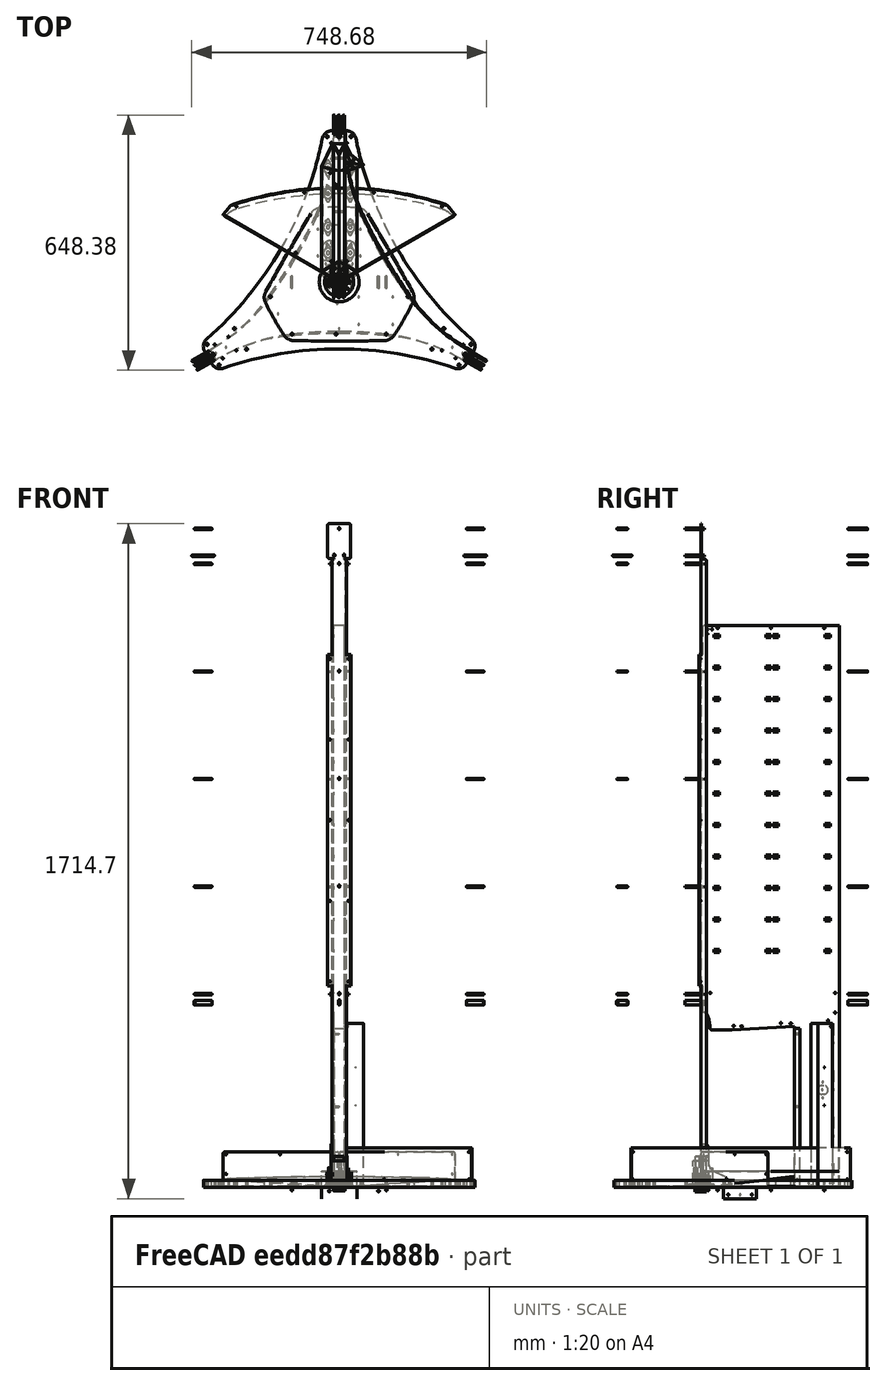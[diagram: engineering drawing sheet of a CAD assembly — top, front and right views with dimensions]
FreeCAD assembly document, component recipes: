
FREECAD ASSEMBLY — COMPONENT RECIPES ("composit_full_size3")

This assembly document has 76 components, labeled P0..P75 below (a component is one placed body or linked part). 73 of them carry a construction recipe — the FreeCAD feature program that regenerates the part from scratch, quoted from this document or its linked companion documents; the rest are supplied as boundary geometry only. No exploded tour is included for this assembly.
NOTE — document 3 of 3 of this assembly tour. The two overview renders and the header above are repeated from document 1; the component sections below continue where the previous document stopped.
COMPONENT P61 — recipe-attached ("basement2_proxy001", modeled in this document).
Construction recipe (the document's own serialized feature program — sketch geometry with constraints, then the solid features built on it; lengths are millimeters unless a unit is written):

FEATURE [PartDesign::SubShapeBinder] Binder004
  BindCopyOnChange = 0
  BindMode = 0
  ClaimChildren = true
  Context = -> Body009 [Binder004.]
  Fuse = false
  MakeFace = true
  Offset = 2
  OffsetFill = false
  OffsetIntersection = false
  OffsetJoinType = 0
  OffsetOpenResult = false
  PartialLoad = false
  Relative = false
  Support = -> [Array002]
  _Version = 2
FEATURE [PartDesign::Pad] Pad004
  Direction = (0,0,1)
  Length = 3
  Length2 = 10
  Profile = -> Binder004
  Suppressed = false
  Type = 0
FEATURE [PartDesign::SubShapeBinder] Binder134
  BindCopyOnChange = 0
  BindMode = 0
  ClaimChildren = false
  Context = -> Body009 [Binder134.]
  Fuse = false
  MakeFace = true
  OffsetFill = false
  OffsetIntersection = false
  OffsetJoinType = 0
  OffsetOpenResult = false
  PartialLoad = false
  Relative = true
  Support = -> [Body007[Pocket112.Sketch178.]]
  _Version = 2
FEATURE [PartDesign::Boolean] Boolean029
  BaseFeature = -> Pad004
  Group = -> [Compound071]
  Suppressed = false
  Type = 1
  UsePlacement = false
FEATURE [PartDesign::CoordinateSystem] Local_CS012  label="basement_bottom_proxy_bottom"
  AttacherType = Attacher::AttachEngine3D
  AttachmentSupport = -> [XY_Plane013]
  MapMode = 5
FEATURE [PartDesign::CoordinateSystem] Local_CS013  label="basement_bottom_proxy_top"
  AttacherType = Attacher::AttachEngine3D
  AttachmentOffset = pos=(0,0,3) rot=(0,0,1;0rad)
  AttachmentSupport = -> [XY_Plane013]
  MapMode = 5
  Placement = pos=(0,0,3) rot=(0,0,1;0rad)
FEATURE [PartDesign::CoordinateSystem] Local_CS016  label="basement_bottom_proxy_pillar_back_LCS"
  AttacherType = Attacher::AttachEngine3D
  AttachmentOffset = pos=(0,384,3) rot=(0,0,-1;3.14159rad)
  AttachmentSupport = -> [XY_Plane013]
  MapMode = 5
  Placement = pos=(0,384,3) rot=(0,0,-1;3.14159rad)
  expr: .AttachmentOffset.Base.y = <<pillar_placement>>.Placement.Base.y
FEATURE [PartDesign::CoordinateSystem] Local_CS023  label="basement_bottom_proxy_pillar_left_LCS"
  AttacherType = Attacher::AttachEngine3D
  AttachmentOffset = pos=(-332.554,-192,3) rot=(0,0,-1;1.0472rad)
  AttachmentSupport = -> [XY_Plane013]
  MapMode = 5
  Placement = pos=(-332.554,-192,3) rot=(0,0,-1;1.0472rad)
  expr: .AttachmentOffset.Base.x = <<pillar_placement>>.Placement.Base.y * cos(210)
  expr: .AttachmentOffset.Base.y = <<pillar_placement>>.Placement.Base.y * sin(210)
FEATURE [PartDesign::CoordinateSystem] Local_CS024  label="basement_bottom_proxy_pillar_right_LCS"
  AttacherType = Attacher::AttachEngine3D
  AttachmentOffset = pos=(332.554,-192,3) rot=(0,0,1;1.0472rad)
  AttachmentSupport = -> [XY_Plane013]
  MapMode = 5
  Placement = pos=(332.554,-192,3) rot=(0,0,1;1.0472rad)
  expr: .AttachmentOffset.Base.x = <<pillar_placement>>.Placement.Base.y * cos(330)
  expr: .AttachmentOffset.Base.y = <<pillar_placement>>.Placement.Base.y * sin(330)
FEATURE [PartDesign::Body] Body009  label="basement_bottom_proxy"
  AllowCompound = false
  Group = -> [Binder004,Pad004,Binder134,Boolean029,Local_CS012,Local_CS013,Local_CS016,Local_CS023,Local_CS024]
  Origin = -> Origin013
  Tip = -> Boolean029
COMPONENT P62 — recipe-attached ("sink_material_0.30ansi001", modeled in this document).
Construction recipe (the document's own serialized feature program — sketch geometry with constraints, then the solid features built on it; lengths are millimeters unless a unit is written):

FEATURE [Sketcher::SketchObject] Sketch037
  ArcFitTolerance = 0
  AttachmentSupport = -> [XY_Plane028]
  FullyConstrained = false
  MakeInternals = false
  MapMode = 5
  sketch-geometry (2):
    g0: LineSegment StartX=0 StartY=0 StartZ=0 EndX=74.4649 EndY=59.2839 EndZ=0
    g1: LineSegment StartX=0 StartY=0 StartZ=0 EndX=-93.8109 EndY=73.3435 EndZ=0
  constraints (2):
    c: Coincident(g0,g-1)
    c: Coincident(g1,g0)
FEATURE [Part::Part2DObjectPython] Line  label="sink_bend_line"  # Draft 2D object (typed FeaturePython)
  Area = 0
  AttachmentOffset = pos=(304.73,175.936,20) rot=(0,0,1;0rad)
  AttachmentSupport = -> [XY_Plane028]
  BendAngle = 6.48542
  ChamferSize = 0
  Closed = false
  End = (0,0,0)
  FaceAngle = 3.2479
  FilletRadius = 0
  Length = 352.44
  MakeFace = true
  MapMode = 5
  Placement = pos=(304.73,175.936,20) rot=(0,0,1;0rad)
  Points = (2) [(0,0,0),(-304.73,-175.936,-20)]
  Start = (304.73,175.936,20)
  Subdivisions = 0
  expr: .AttachmentOffset.Base.x = Spreadsheet.total_length * cos(30)
  expr: .AttachmentOffset.Base.y = Spreadsheet.total_length * sin(30)
  expr: BendAngle = atan2(.AttachmentOffset.Base.z; .AttachmentOffset.Base.y)
  expr: End = tuple(0; 0; 0)
  expr: FaceAngle = atan2(.AttachmentOffset.Base.z; Length)
FEATURE [PartDesign::Line] DatumLine
  AttacherType = Attacher::AttachEngineLine
  AttachmentSupport = -> [Z_Axis028]
  Length = 20
  MapMode = 29
  ResizeMode = 0
FEATURE [PartDesign::Line] DatumLine001
  AttacherType = Attacher::AttachEngineLine
  AttachmentSupport = -> [Line,X_Axis028]
  Length = 20
  MapMode = 24
  Placement = pos=(304.73,175.936,20) rot=(0.57735,-0.57735,-0.57735;2.0944rad)
  ResizeMode = 0
FEATURE [Sketcher::SketchObject] Sketch038
  ArcFitTolerance = 0
  AttachmentSupport = -> [Line]
  ExternalGeometry = -> [DatumLine001]
  FullyConstrained = false
  MakeInternals = false
  MapMode = 45
  Placement = pos=(152.365,87.9679,10) rot=(0.368581,0.6384,0.675717;2.39766rad)
  sketch-geometry (3):
    g0: LineSegment StartX=4.75e-14 StartY=4.27e-14 StartZ=0 EndX=4.75e-14 EndY=93.8582 EndZ=0
    g1: LineSegment StartX=4.75e-14 StartY=4.27e-14 StartZ=0 EndX=35.2298 EndY=3.46271 EndZ=0
    g2: ArcOfCircle CenterX=2.5 CenterY=2.75777 CenterZ=0 NormalX=0 NormalY=0 NormalZ=1 AngleXU=0 Radius=2.5 StartAngle=3.14159 EndAngle=4.81036
  constraints (9):
    c: Coincident(g0,g-1)
    c: Vertical(g0)
    c: Coincident(g1,g0)
    c: PointOnObject(g1,g-3)
    c: Angle(g-3) = 0.0979746
    c: Angle(g1,g0) = 1.47282  'bend_angle'
    c: Tangent(g2,g0) = 1.5708
    c: Tangent(g2,g1) = -1.5708
    c: Radius(g2) = 2.5
FEATURE [PartDesign::CoordinateSystem] Local_CS
  AttacherType = Attacher::AttachEngine3D
  AttachmentOffset = pos=(0,0,0) rot=(1,0,0;0.113192rad)
  AttachmentSupport = -> [XY_Plane028]
  MapMode = 5
  Placement = pos=(0,0,0) rot=(1,0,0;0.113192rad)
  expr: .AttachmentOffset.Rotation.Angle = Line.BendAngle
FEATURE [Sketcher::SketchObject] Sketch039
  ArcFitTolerance = 0
  AttachmentSupport = -> [Local_CS]
  ExternalGeometry = -> [Line,Sketch038]
  FullyConstrained = true
  MakeInternals = false
  MapMode = 5
  Placement = pos=(0,0,0) rot=(1,0,0;0.113192rad)
  sketch-geometry (3):
    g0: LineSegment StartX=2e-16 StartY=3.18954 StartZ=0 EndX=-459.172 EndY=270 EndZ=0
    g1: LineSegment StartX=2e-16 StartY=3.18954 StartZ=0 EndX=459.172 EndY=270 EndZ=0
    g2: LineSegment StartX=459.172 StartY=270 StartZ=0 EndX=-459.172 EndY=270 EndZ=0
  constraints (8):
    c: Coincident(g2,g1)
    c: DistanceY(g1) = 270
    c: Coincident(g0,g2)
    c: Symmetric(g1,g0,g-2)
    c: Coincident(g1,g0)
    c: PointOnObject(g0,g-2)
    c: Parallel(g1,g-3)
    c: PointOnObject(g-4,g1)
FEATURE [PartDesign::FeaturePython] BaseBend011  # WARN: FeaturePython — macro-defined, semantics opaque (R4)
  BendSide = 0
  BendSketch = -> Sketch039
  MidPlane = false
  Reverse = false
  Suppressed = false
  length = 100
  radius = 2
  thickness = 0.5
FEATURE [PartDesign::FeaturePython] Bend004  # WARN: FeaturePython — macro-defined, semantics opaque (R4)
  AutoMiter = false
  BaseFeature = -> BaseBend011
  BendType = 0
  LengthList = [100]
  LengthSpec = 1
  NonperforationMaxLength = 5
  Perforate = false
  PerforationAngle = 0
  PerforationInitialLength = 5
  PerforationMaxLength = 5
  ReliefFactor = 0.7
  Suppressed = false
  UseReliefFactor = false
  angle = 95.6135
  baseObject = -> BaseBend011 [Edge3,Edge8]
  bendAList = [95.6135]
  extend1 = 2
  extend2 = 0
  gap1 = 0
  gap2 = 0
  invert = true
  kfactor = 0.5
  length = 100
  maxExtendDist = 5
  minGap = 0.1
  minReliefGap = 1
  miterangle1 = 0
  miterangle2 = 0
  offset = 0
  radius = 2
  reliefType = 0
  reliefd = 1
  reliefw = 0.8
  sketchflip = false
  sketchinvert = false
  unfold = false
  expr: angle = 180 deg - Sketch038.Constraints.bend_angle
  expr: radius = BaseBend011.radius
FEATURE [Sketcher::SketchObject] Sketch040
  ArcFitTolerance = 0
  AttachmentSupport = -> [Local_CS]
  ExternalGeometry = -> [Line,Sketch038]
  FullyConstrained = true
  MakeInternals = false
  MapMode = 5
  Placement = pos=(0,0,0) rot=(1,0,0;0.113192rad)
  sketch-geometry (13):
    g0: ArcOfCircle CenterX=0 CenterY=-630 CenterZ=0 NormalX=0 NormalY=0 NormalZ=1 AngleXU=0 Radius=870 StartAngle=1.24863 EndAngle=1.89296
    g1: LineSegment [constr] StartX=0 StartY=0 StartZ=0 EndX=294.959 EndY=171.391 EndZ=0
    g2: LineSegment [constr] StartX=150.979 StartY=90.9189 StartZ=0 EndX=293.573 EndY=173.776 EndZ=0
    g3: LineSegment [constr] StartX=-294.959 StartY=171.391 StartZ=0 EndX=0 EndY=0 EndZ=0
    g4: LineSegment StartX=-294.959 StartY=171.391 StartZ=0 EndX=-464.661 EndY=270 EndZ=0
    g5: LineSegment StartX=-464.661 StartY=270 StartZ=0 EndX=464.661 EndY=270 EndZ=0
    g6: LineSegment StartX=464.661 StartY=270 StartZ=0 EndX=294.959 EndY=171.391 EndZ=0
    g7: LineSegment StartX=294.959 StartY=171.391 StartZ=0 EndX=294.075 EndY=172.911 EndZ=0
    g8: LineSegment StartX=294.075 StartY=172.911 StartZ=0 EndX=293.573 EndY=173.776 EndZ=0
    g9: LineSegment [constr] StartX=-294.959 StartY=171.391 StartZ=0 EndX=-294.959 EndY=171.391 EndZ=0
    g10: LineSegment StartX=293.573 StartY=173.776 StartZ=0 EndX=275.46 EndY=195.241 EndZ=0
    g11: LineSegment StartX=-293.573 StartY=173.776 StartZ=0 EndX=-275.46 EndY=195.241 EndZ=0
    g12: LineSegment StartX=-294.959 StartY=171.391 StartZ=0 EndX=-293.573 EndY=173.776 EndZ=0
  constraints (34):
    c: Coincident(g1,g-1)
    c: PointOnObject(g1,g-3)
    c: Coincident(g7,g1)
    c: Distance(g1) = 341.139
    c: Coincident(g2,g-4)
    c: Parallel(g2,g1)
    c: DistanceY(g0) = -630
    c: Radius(g0) = 870
    c: Coincident(g9,g3)
    c: Coincident(g3,g1)
    c: Symmetric(g9,g7,g-2)
    c: Coincident(g4,g5)
    c: Coincident(g5,g6)
    c: Parallel(g6,g2)
    c: Symmetric(g5,g4,g-2)
    c: DistanceY(g5) = 270
    c: Coincident(g2,g8)
    c: Coincident(g7,g8)
    c: Perpendicular(g1,g7)
    c: Perpendicular(g1,g8)
    c: Distance(g8) = 1
    c: Coincident(g10,g0)
    c: Coincident(g11,g0)
    c: PointOnObject(g0,g-2)
    c: Coincident(g10,g8)
    c: Coincident(g12,g9)
    c: Coincident(g4,g12)
    c: Coincident(g12,g11)
    c: Symmetric(g4,g6,g-2)
    c: Symmetric(g8,g11,g-2)
    c: Horizontal(g0,g0)
    c: Distance(g10) = 28.0862
    c: Angle(g10,g2) = 1.39626
    c: Coincident(g6,g7)
FEATURE [PartDesign::SubShapeBinder] Binder031
  BindCopyOnChange = 0
  BindMode = 0
  ClaimChildren = false
  Context = -> Part007 [Body020.Binder031.]
  Fuse = false
  MakeFace = true
  OffsetFill = false
  OffsetIntersection = false
  OffsetJoinType = 0
  OffsetOpenResult = false
  PartialLoad = false
  Relative = true
  _Version = 2
FEATURE [PartDesign::Pocket] Pocket022
  BaseFeature = -> Bend004
  Direction = (0,0.11295,-0.993601)
  Length = 2.5
  Length2 = 5
  Profile = -> Sketch040
  ReferenceAxis = -> Sketch040 [N_Axis]
  Refine = true
  Reversed = true
  Suppressed = false
  Type = 0
FEATURE [Sketcher::SketchObject] Sketch042
  ArcFitTolerance = 0
  AttachmentSupport = -> [XY_Plane028]
  FullyConstrained = true
  MakeInternals = false
  MapMode = 5
  sketch-geometry (7):
    g0: LineSegment StartX=-18.3205 StartY=-10 StartZ=0 EndX=-0.5 EndY=0.288675 EndZ=0
    g1: LineSegment StartX=18.3205 StartY=-10 StartZ=0 EndX=-18.3205 EndY=-10 EndZ=0
    g2: LineSegment [constr] StartX=1 StartY=1.5e-15 StartZ=0 EndX=-1e-16 EndY=0.57735 EndZ=0
    g3: LineSegment [constr] StartX=1.3e-15 StartY=-2.2e-15 StartZ=0 EndX=0.5 EndY=0.288675 EndZ=0
    g4: LineSegment StartX=0.5 StartY=0.288675 StartZ=0 EndX=18.3205 EndY=-10 EndZ=0
    g5: LineSegment StartX=-2.6e-15 StartY=1.1547 StartZ=0 EndX=0.5 EndY=0.288675 EndZ=0
    g6: LineSegment StartX=-0.5 StartY=0.288675 StartZ=0 EndX=-2.6e-15 EndY=1.1547 EndZ=0
  constraints (19):
    c: Coincident(g4,g1)
    c: Coincident(g1,g0)
    c: Symmetric(g4,g0,g-2)
    c: PointOnObject(g2,g-1)
    c: PointOnObject(g2,g-2)
    c: Angle(g2) = 2.61799
    c: Distance(g-1,g2) = 0.5
    c: Coincident(g3,g-1)
    c: PointOnObject(g3,g2)
    c: Angle(g3) = 0.523599
    c: PointOnObject(g2,g4)
    c: Perpendicular(g3,g5)
    c: Coincident(g4,g5)
    c: Coincident(g4,g3)
    c: PointOnObject(g5,g-2)
    c: Coincident(g6,g0)
    c: Coincident(g6,g5)
    c: Symmetric(g4,g0,g-2)
    c: DistanceY(g1) = -10
FEATURE [Sketcher::SketchObject] Sketch041
  ArcFitTolerance = 0
  AttachmentOffset = pos=(0,0,0) rot=(0,1,0;0.523599rad)
  AttachmentSupport = -> [XZ_Plane028]
  ExternalGeometry = -> [Sketch038,Sketch042,Sketch040]
  FullyConstrained = false
  MakeInternals = false
  MapMode = 5
  Placement = pos=(0,0,0) rot=(0.935113,0.250563,0.250563;1.63783rad)
  sketch-geometry (16):
    g0: LineSegment StartX=340.573 StartY=19.628 StartZ=0 EndX=340.432 EndY=22.112 EndZ=0
    g1: LineSegment [constr] StartX=175.779 StartY=12.7533 StartZ=0 EndX=340.432 EndY=22.112 EndZ=0
    g2: LineSegment StartX=0.57735 StartY=196.491 StartZ=0 EndX=638.392 EndY=196.491 EndZ=0
    g3: LineSegment StartX=638.392 StartY=196.491 StartZ=0 EndX=638.392 EndY=36.5557 EndZ=0
    g4: LineSegment StartX=638.392 StartY=36.5557 StartZ=0 EndX=340.573 EndY=19.628 EndZ=0
    g5: LineSegment StartX=340.432 StartY=22.112 StartZ=0 EndX=340.432 EndY=85 EndZ=0
    g6: LineSegment StartX=0.57735 StartY=85 StartZ=0 EndX=0.57735 EndY=196.491 EndZ=0
    g7: LineSegment StartX=335.432 StartY=90 StartZ=0 EndX=5.57735 EndY=90 EndZ=0
    g8: ArcOfCircle CenterX=5.57735 CenterY=85 CenterZ=0 NormalX=0 NormalY=0 NormalZ=1 AngleXU=0 Radius=5 StartAngle=1.5708 EndAngle=3.14159
    g9: ArcOfCircle CenterX=335.432 CenterY=85 CenterZ=0 NormalX=0 NormalY=0 NormalZ=1 AngleXU=0 Radius=5 StartAngle=2e-16 EndAngle=1.5708
    g10: GeomPoint [constr] X=340.432 Y=90 Z=0
    g11: LineSegment StartX=0.57735 StartY=0 StartZ=0 EndX=0.57735 EndY=27.6603 EndZ=0
    g12: ArcOfCircle CenterX=5 CenterY=27.6603 CenterZ=0 NormalX=0 NormalY=0 NormalZ=1 AngleXU=0 Radius=4.42265 StartAngle=3.14159 EndAngle=4.18879
    g13: ArcOfCircle CenterX=0.57735 CenterY=20 CenterZ=0 NormalX=0 NormalY=0 NormalZ=1 AngleXU=0 Radius=4.42265 StartAngle=-2.31e-14 EndAngle=1.0472
    g14: LineSegment StartX=5 StartY=20 StartZ=0 EndX=5 EndY=0 EndZ=0
    g15: LineSegment StartX=5 StartY=0 StartZ=0 EndX=0.57735 EndY=0 EndZ=0
  constraints (39):
    c: Coincident(g1,g-3)
    c: Coincident(g1,g0)
    c: Perpendicular(g-3,g1)
    c: Perpendicular(g1,g0)
    c: Coincident(g5,g0)
    c: Coincident(g6,g2)
    c: Horizontal(g2)
    c: Coincident(g2,g3)
    c: Vertical(g3)
    c: Coincident(g3,g4)
    c: Coincident(g4,g0)
    c: Parallel(g4,g1)
    c: Vertical(g5)
    c: Vertical(g6)
    c: Vertical(g6,g-4)
    c: Horizontal(g7)
    c: Tangent(g8,g7) = -1.5708
    c: Tangent(g8,g6) = 1.5708
    c: PointOnObject(g10,g5)
    c: PointOnObject(g10,g7)
    c: Tangent(g5,g9) = -1.5708
    c: Tangent(g7,g9) = -1.5708
    c: Equal(g9,g8)
    c: Coincident(g11,g-4)
    c: Vertical(g11)
    c: PointOnObject(g13,g11)
    c: PointOnObject(g14,g-1)
    c: Vertical(g14)
    c: Coincident(g15,g14)
    c: Coincident(g15,g11)
    c: Tangent(g13,g12) = 1.5708
    c: Tangent(g12,g11) = 1.5708
    c: Tangent(g14,g13) = 1.5708
    c: Equal(g13,g12)
    c: DistanceX(g14) = 5
    c: DistanceY(g13) = 20
    c: DistanceY(g7) = 90
    c: Radius(g9) = 5
    c: Coincident(g0,g-5)
FEATURE [Sketcher::SketchObject] Sketch043
  ArcFitTolerance = 0
  AttachmentSupport = -> [Local_CS]
  FullyConstrained = false
  MakeInternals = false
  MapMode = 5
  Placement = pos=(0,0,0) rot=(1,0,0;0.113192rad)
  expr: Constraints[12] = Sketch038.Constraints.bend_angle / 2
  sketch-geometry (7):
    g0: ArcOfCircle CenterX=-2.2e-14 CenterY=1.72e-14 CenterZ=0 NormalX=0 NormalY=0 NormalZ=1 AngleXU=0 Radius=19.4106 StartAngle=5.52221 EndAngle=10.1858
    g1: ArcOfCircle CenterX=17.4885 CenterY=-16.6545 CenterZ=0 NormalX=0 NormalY=0 NormalZ=1 AngleXU=0 Radius=4.73935 StartAngle=2.38062 EndAngle=3.72466
    g2: ArcOfCircle CenterX=-17.4885 CenterY=-16.6545 CenterZ=0 NormalX=0 NormalY=0 NormalZ=1 AngleXU=0 Radius=4.73935 StartAngle=5.70012 EndAngle=7.04416
    g3: LineSegment StartX=13.5322 StartY=-19.2639 StartZ=0 EndX=49.1398 EndY=-73.2508 EndZ=0
    g4: LineSegment StartX=-13.5322 StartY=-19.2639 StartZ=0 EndX=-49.1398 EndY=-73.2508 EndZ=0
    g5: LineSegment StartX=-49.1398 StartY=-73.2508 StartZ=0 EndX=49.1398 EndY=-73.2508 EndZ=0
    g6: LineSegment StartX=-86.3387 StartY=-141.994 StartZ=0 EndX=130.665 EndY=54.7259 EndZ=0
  constraints (13):
    c: Coincident(g0,g-1)
    c: Coincident(g5,g4)
    c: Coincident(g5,g3)
    c: Tangent(g3,g1) = -1.5708
    c: Tangent(g1,g0) = 1.5708
    c: Tangent(g2,g0) = 1.5708
    c: Tangent(g4,g2) = 1.5708
    c: Symmetric(g4,g3,g-2)
    c: Symmetric(g2,g1,g-2)
    c: DistanceX(g1) = 13.5322
    c: DistanceY(g1) = -19.2639
    c: Angle(g3) = -0.987729
    c: Angle(g6) = 0.736411
FEATURE [Sketcher::SketchObject] Sketch064
  ArcFitTolerance = 0
  AttachmentSupport = -> [Local_CS]
  FullyConstrained = true
  MakeInternals = false
  MapMode = 5
  Placement = pos=(0,0,0) rot=(1,0,0;0.113192rad)
  expr: Constraints[3] = <<Properties>>.rivet_d
  sketch-geometry (4):
    g0: Circle CenterX=-88.3 CenterY=228.865 CenterZ=0 NormalX=0 NormalY=0 NormalZ=1 AngleXU=0 Radius=1.7
    g1: Circle CenterX=88.3 CenterY=228.865 CenterZ=0 NormalX=0 NormalY=0 NormalZ=1 AngleXU=0 Radius=1.7
    g2: Circle CenterX=261.291 CenterY=193.3 CenterZ=0 NormalX=0 NormalY=0 NormalZ=1 AngleXU=0 Radius=1.7
    g3: Circle CenterX=-261.291 CenterY=193.3 CenterZ=0 NormalX=0 NormalY=0 NormalZ=1 AngleXU=0 Radius=1.7
  constraints (10):
    c: Equal(g2,g1)
    c: Equal(g2,g0)
    c: Equal(g2,g3)
    c: Diameter(g2) = 3.4
    c: DistanceX(g1) = 88.3
    c: DistanceY(g1) = 228.865
    c: DistanceX(g2) = 261.291
    c: DistanceY(g2) = 193.3
    c: Symmetric(g0,g1,g-2)
    c: Symmetric(g3,g2,g-2)
FEATURE [Sketcher::SketchObject] Sketch219
  ArcFitTolerance = 0
  FullyConstrained = false
  MakeInternals = false
  MapMode = 5
  Placement = pos=(0,8e-15,-6.7e-14) rot=(1,0,0;3.25479rad)
  sketch-geometry (6):
    g0: LineSegment StartX=297.803 StartY=-177.345 StartZ=0 EndX=303.917 EndY=-182.504 EndZ=0
    g1: LineSegment StartX=303.917 StartY=-182.504 StartZ=0 EndX=285.803 EndY=-203.969 EndZ=0
    g2: LineSegment StartX=285.803 StartY=-203.969 StartZ=0 EndX=276.608 EndY=-196.209 EndZ=0
    g3: LineSegment StartX=279.192 StartY=-196.205 StartZ=0 EndX=297.807 EndY=-180.398 EndZ=0
    g4: ArcOfCircle CenterX=296.513 CenterY=-178.873 CenterZ=0 NormalX=0 NormalY=0 NormalZ=1 AngleXU=0 Radius=2 StartAngle=5.41641 EndAngle=7.15307
    g5: ArcOfCircle CenterX=277.898 CenterY=-194.681 CenterZ=0 NormalX=0 NormalY=0 NormalZ=1 AngleXU=0 Radius=2 StartAngle=4.01147 EndAngle=5.41641
  constraints (13):
    c: Coincident(g0,g1)
    c: Coincident(g1,g2)
    c: Perpendicular(g1,g2)
    c: Perpendicular(g0,g1)
    c: Tangent(g4,g0) = 1.5708
    c: Tangent(g5,g2) = 1.5708
    c: Tangent(g5,g3) = -1.5708
    c: Tangent(g4,g3) = -1.5708
    c: Equal(g4,g5)
    c: Radius(g4) = 2
    c: Distance(g0) = 8
    c: Distance(g2) = 12.0319
    c: Distance(g3,g1) = 10.0593
FEATURE [PartDesign::FeaturePython] Bend033  # WARN: FeaturePython — macro-defined, semantics opaque (R4)
  AutoMiter = true
  BaseFeature = -> Pocket022
  BendType = 0
  LengthList = [10]
  LengthSpec = 0
  NonperforationMaxLength = 5
  Perforate = false
  PerforationAngle = 0
  PerforationInitialLength = 5
  PerforationMaxLength = 5
  ReliefFactor = 0.7
  Suppressed = false
  UseReliefFactor = false
  angle = 90
  baseObject = -> Pocket022 [Edge64,Edge69]
  bendAList = [90]
  extend1 = 0
  extend2 = 0
  gap1 = 0
  gap2 = 0
  invert = false
  kfactor = 0.5
  length = 10
  maxExtendDist = 5
  minGap = 0.2
  minReliefGap = 1
  miterangle1 = 0
  miterangle2 = 0
  offset = 0
  radius = 2
  reliefType = 0
  reliefd = 1
  reliefw = 0.8
  sketchflip = false
  sketchinvert = false
  unfold = true
  expr: radius = BaseBend011.radius
FEATURE [PartDesign::Pocket] Pocket131
  BaseFeature = -> Bend033
  Direction = (0,-0.11295,0.993601)
  Length = 5
  Length2 = 5
  Profile = -> Sketch219
  ReferenceAxis = -> Sketch219 [N_Axis]
  Suppressed = false
  Type = 0
FEATURE [PartDesign::Mirrored] Mirrored017
  BaseFeature = -> Pocket131
  MirrorPlane = -> YZ_Plane028
  Originals = -> [Pocket131]
  Suppressed = false
  TransformMode = 0
FEATURE [PartDesign::Pocket] Pocket024
  BaseFeature = -> Mirrored017
  Direction = (0,0,-1)
  Length = 5
  Length2 = 5
  Midplane = true
  Profile = -> Sketch042
  ReferenceAxis = -> Sketch042 [N_Axis]
  Suppressed = false
  Type = 1
FEATURE [PartDesign::FeaturePython] CornerRelief  # WARN: FeaturePython — macro-defined, semantics opaque (R4)
  BaseFeature = -> Pocket024
  ReliefSketch = 0
  Size = 6
  SizeRatio = 1.5
  Sketch = -> Sketch043
  Suppressed = false
  XOffset = 0
  YOffset = 0
  baseObject = -> Pocket024 [Edge35,Edge16]
  kfactor = 0.5
FEATURE [PartDesign::Pocket] Pocket023
  BaseFeature = -> CornerRelief
  Direction = (-0.5,0.866025,-1e-16)
  Length = 0.6
  Length2 = 5
  Profile = -> Sketch041
  ReferenceAxis = -> Sketch041 [N_Axis]
  Suppressed = false
  Type = 0
FEATURE [PartDesign::Mirrored] Mirrored002
  BaseFeature = -> Pocket023
  MirrorPlane = -> YZ_Plane028
  Originals = -> [Pocket023]
  Refine = true
  Suppressed = false
  TransformMode = 0
FEATURE [PartDesign::Boolean] Boolean008
  BaseFeature = -> Mirrored002
  Group = -> [Compound028]
  Suppressed = false
  Type = 1
  UsePlacement = false
  expr: Group = <<sink_fix001>>._self
FEATURE [PartDesign::Pocket] Pocket029
  BaseFeature = -> Boolean008
  Direction = (0,0.11295,-0.993601)
  Length = 5
  Length2 = 5
  Profile = -> Sketch064
  ReferenceAxis = -> Sketch064 [N_Axis]
  Reversed = true
  Suppressed = false
  Type = 1
FEATURE [PartDesign::Body] Body020  label="sink_material_0.30ansi"
  AllowCompound = false
  Group = -> [Sketch037,Line,DatumLine,Sketch038,DatumLine001,Sketch039,BaseBend011,Bend004,Local_CS,Sketch040,Binder031,Pocket022,Sketch041,Sketch042,Sketch219,Bend033,Pocket131,Mirrored017,Pocket024,Sketch043,CornerRelief,Pocket023,Mirrored002,Boolean008,Sketch064,Pocket029]
  Origin = -> Origin028
  Tip = -> Pocket029
COMPONENT P63 — recipe-attached ("Body110", modeled in this document).
Construction recipe (the document's own serialized feature program — sketch geometry with constraints, then the solid features built on it; lengths are millimeters unless a unit is written):

FEATURE [PartDesign::SubShapeBinder] Binder061
  BindCopyOnChange = 0
  BindMode = 0
  ClaimChildren = false
  Context = -> Part007 [Body021.Binder061.]
  Fuse = false
  MakeFace = true
  OffsetFill = false
  OffsetIntersection = false
  OffsetJoinType = 0
  OffsetOpenResult = false
  PartialLoad = false
  Relative = false
  Support = -> [Body020[Pocket022.Sketch040.]]
  _Version = 2
FEATURE [PartDesign::SubShapeBinder] Binder062
  BindCopyOnChange = 0
  BindMode = 0
  ClaimChildren = false
  Context = -> Part007 [Body021.Binder062.]
  Fuse = false
  MakeFace = true
  OffsetFill = false
  OffsetIntersection = false
  OffsetJoinType = 0
  OffsetOpenResult = false
  PartialLoad = false
  Relative = false
  Support = -> [Body020[Pocket029.Sketch064.]]
  _Version = 2
FEATURE [Sketcher::SketchObject] Sketch109
  ArcFitTolerance = 0
  AttachmentSupport = -> [XY_Plane029]
  ExternalGeometry = -> [Binder061]
  FullyConstrained = false
  MakeInternals = false
  MapMode = 5
  sketch-geometry (19):
    g0: ArcOfCircle CenterX=291.996 CenterY=172.865 CenterZ=0 NormalX=0 NormalY=0 NormalZ=1 AngleXU=0 Radius=1 StartAngle=5.23599 EndAngle=6.98132
    g1: LineSegment StartX=5.51e-14 StartY=239 StartZ=0 EndX=5.51e-14 EndY=240 EndZ=0
    g2: LineSegment StartX=292.496 StartY=171.999 StartZ=0 EndX=287.719 EndY=169.241 EndZ=0
    g3: ArcOfCircle CenterX=287.219 CenterY=170.107 CenterZ=0 NormalX=0 NormalY=0 NormalZ=1 AngleXU=0 Radius=1 StartAngle=3.90153 EndAngle=5.23599
    g4: LineSegment StartX=5.51e-14 StartY=239 StartZ=0 EndX=5.51e-14 EndY=224 EndZ=0
    g5: ArcOfCircle CenterX=243.002 CenterY=128.086 CenterZ=0 NormalX=0 NormalY=0 NormalZ=1 AngleXU=0 Radius=60 StartAngle=0.759936 EndAngle=1.27733
    g6: GeomPoint [constr] X=287.033 Y=168.845 Z=0
    g7: GeomPoint [constr] X=293.528 Y=172.595 Z=0
    g8: ArcOfCircle CenterX=1.26657 CenterY=-621.999 CenterZ=0 NormalX=0 NormalY=0 NormalZ=1 AngleXU=0 Radius=862 StartAngle=1.25533 EndAngle=1.57227
    g9: LineSegment [constr] StartX=5.28e-14 StartY=220.8 StartZ=0 EndX=5.51e-14 EndY=240 EndZ=0
    g10: ArcOfCircle [constr] CenterX=0 CenterY=-641.2 CenterZ=0 NormalX=0 NormalY=0 NormalZ=1 AngleXU=0 Radius=862 StartAngle=1.25386 EndAngle=1.5708
    g11: LineSegment [constr] StartX=5.51e-14 StartY=240 StartZ=0 EndX=268.713 EndY=197.462 EndZ=0
    g12: LineSegment [constr] StartX=5.28e-14 StartY=220.8 StartZ=0 EndX=268.65 EndY=177.867 EndZ=0
    g13: ArcOfCircle CenterX=0 CenterY=-676.059 CenterZ=0 NormalX=0 NormalY=0 NormalZ=1 AngleXU=0 Radius=900.059 StartAngle=1.27733 EndAngle=1.5708
    g14: Circle [constr] CenterX=268.65 CenterY=177.867 CenterZ=0 NormalX=0 NormalY=0 NormalZ=1 AngleXU=0 Radius=4
    g15: LineSegment [constr] StartX=0 StartY=0 StartZ=0 EndX=301.632 EndY=174.148 EndZ=0
    g16: LineSegment [constr] StartX=0 StartY=0 StartZ=0 EndX=-15 EndY=25.9808 EndZ=0
    g17: ArcOfCircle CenterX=262.507 CenterY=178.449 CenterZ=0 NormalX=0 NormalY=0 NormalZ=1 AngleXU=0 Radius=20 StartAngle=0.698132 EndAngle=1.25533
    g18: LineSegment StartX=292.762 StartY=173.508 StartZ=0 EndX=277.828 EndY=191.305 EndZ=0
  constraints (51):
    c: Tangent(g17,g8) = -1.5708
    c: Vertical(g1)
    c: PointOnObject(g1,g-2)
    c: Angle(g2) = -2.61799
    c: Tangent(g2,g0) = 1.5708
    c: DistanceY(g1,g1) = 1
    c: Tangent(g3,g2) = 1.5708
    c: Radius(g3) = 1
    c: Equal(g3,g0)
    c: Coincident(g4,g1)
    c: Vertical(g4)
    c: Distance(g4) = 15
    c: Tangent(g5,g3) = 1.5708
    c: PointOnObject(g7,g2)
    c: PointOnObject(g6,g2)
    c: PointOnObject(g6,g5)
    c: Coincident(g8,g1)
    c: PointOnObject(g9,g-2)
    c: DistanceY(g9,g4) = 3.2
    c: Coincident(g9,g1)
    c: Radius(g8) = 862  'outer_r'
    c: Distance(g6,g7) = 7.5
    c: PointOnObject(g10,g-2)
    c: Coincident(g11,g1)
    c: Coincident(g11,g17)
    c: Coincident(g12,g10)
    c: Coincident(g12,g10)
    c: Equal(g10,g8)
    c: Equal(g12,g11)
    c: Coincident(g10,g9)
    c: PointOnObject(g13,g-2)
    c: Coincident(g13,g4)
    c: Tangent(g13,g5) = -1.5708
    c: Coincident(g14,g10)
    c: Tangent(g14,g5)
    c: Radius(g14) = 4
    c: Coincident(g15,g-1)
    c: Angle(g15) = 0.523599
    c: Distance(g6,g15) = 2.7076
    c: DistanceY(g1) = 240
    c: Coincident(g16,g15)
    c: Perpendicular(g15,g16)
    c: Distance(g7,g16) = 340.5
    c: Tangent(g18,g0) = -1.5708
    c: Angle(g18) = 2.26893
    c: Tangent(g17,g18) = -1.5708
    c: PointOnObject(g8,g-5)
    c: Radius(g17) = 20
    c: PointOnObject(g7,g18)
    c: Radius(g5) = 60
    c: Distance(g16) = 30
FEATURE [PartDesign::Pad] Pad014
  Direction = (0,0,1)
  Length = 3
  Length2 = 10
  Profile = -> Sketch109
  ReferenceAxis = -> Sketch109 [N_Axis]
  Suppressed = false
  Type = 0
FEATURE [PartDesign::Mirrored] Mirrored008
  BaseFeature = -> Pad014
  MirrorPlane = -> Sketch109 [V_Axis]
  Originals = -> [Pad014]
  Refine = true
  Suppressed = false
  TransformMode = 0
FEATURE [PartDesign::Pocket] Pocket055
  BaseFeature = -> Mirrored008
  Direction = (0,0,-1)
  Length = 5
  Length2 = 5
  Profile = -> Binder062
  Reversed = true
  Suppressed = false
  Type = 0
FEATURE [PartDesign::Body] Body021
  AllowCompound = false
  Group = -> [Binder061,Binder062,Sketch109,Pad014,Mirrored008,Pocket055]
  Origin = -> Origin029
  Placement = pos=(0,0,0) rot=(1,0,0;0.116239rad)
  Tip = -> Pocket055
COMPONENT P64 — recipe-attached ("hat003", modeled in this document).
Construction recipe (the document's own serialized feature program — sketch geometry with constraints, then the solid features built on it; lengths are millimeters unless a unit is written):

FEATURE [PartDesign::SubShapeBinder] Binder041
  BindCopyOnChange = 0
  BindMode = 0
  ClaimChildren = true
  Context = -> Body076 [Binder041.]
  Fuse = false
  MakeFace = true
  OffsetFill = false
  OffsetIntersection = false
  OffsetJoinType = 0
  OffsetOpenResult = false
  PartialLoad = false
  Relative = false
  Support = -> [Array006]
  _Version = 2
FEATURE [PartDesign::Pad] Pad010
  Direction = (0,0,1)
  Length = 0.3
  Length2 = 10
  Profile = -> Binder041
  Suppressed = false
  Type = 0
FEATURE [Sketcher::SketchObject] Sketch072
  ArcFitTolerance = 0
  AttachmentSupport = -> [XY_Plane039]
  FullyConstrained = true
  MakeInternals = false
  MapMode = 5
  sketch-geometry (3):
    g0: Circle CenterX=122.567 CenterY=-102.846 CenterZ=0 NormalX=0 NormalY=0 NormalZ=1 AngleXU=0 Radius=15
    g1: Circle CenterX=-122.567 CenterY=-102.846 CenterZ=0 NormalX=0 NormalY=0 NormalZ=1 AngleXU=0 Radius=15
    g2: LineSegment [constr] StartX=0 StartY=0 StartZ=0 EndX=122.567 EndY=-102.846 EndZ=0
  constraints (7):
    c: Coincident(g2,g-1)
    c: Coincident(g2,g0)
    c: Angle(g2) = -0.698132
    c: Symmetric(g1,g0,g-2)
    c: Equal(g0,g1)
    c: Distance(g2) = 160
    c: Diameter(g0) = 30
FEATURE [PartDesign::Boolean] Boolean063
  BaseFeature = -> Pad010
  Group = -> [Compound116]
  Suppressed = false
  Type = 1
  UsePlacement = false
FEATURE [PartDesign::FeaturePython] Bend032  # WARN: FeaturePython — macro-defined, semantics opaque (R4)
  AutoMiter = true
  BaseFeature = -> Boolean063
  BendType = 0
  LengthList = [25]
  LengthSpec = 0
  NonperforationMaxLength = 5
  Perforate = false
  PerforationAngle = 0
  PerforationInitialLength = 5
  PerforationMaxLength = 5
  ReliefFactor = 0.7
  Suppressed = false
  UseReliefFactor = false
  angle = 90
  baseObject = -> Boolean063 [Edge33,Edge35]
  bendAList = [90]
  extend1 = 0
  extend2 = 0
  gap1 = 3.2
  gap2 = 3.2
  invert = false
  kfactor = 0.5
  length = 25
  maxExtendDist = 5
  minGap = 0.2
  minReliefGap = 1
  miterangle1 = 0
  miterangle2 = 0
  offset = 0
  radius = 0.1
  reliefType = 0
  reliefd = 1
  reliefw = 0.8
  sketchflip = false
  sketchinvert = false
  unfold = false
FEATURE [PartDesign::Boolean] Boolean064
  BaseFeature = -> Bend032
  Group = -> [Fusion011]
  Suppressed = false
  Type = 1
  UsePlacement = false
FEATURE [PartDesign::Body] Body076  label="hat_top"
  AllowCompound = false
  Group = -> [Binder041,Pad010,Sketch072,Boolean063,Bend032,Boolean064]
  Origin = -> Origin039
  Placement = pos=(0,0,87) rot=(0,0,1;0rad)
  Tip = -> Boolean064
COMPONENT P65 — recipe-attached ("hat004", modeled in this document).
Construction recipe (the document's own serialized feature program — sketch geometry with constraints, then the solid features built on it; lengths are millimeters unless a unit is written):

FEATURE [PartDesign::SubShapeBinder] Binder039
  BindCopyOnChange = 0
  BindMode = 0
  ClaimChildren = true
  Context = -> Body075 [Binder039.]
  Fuse = false
  MakeFace = true
  OffsetFill = false
  OffsetIntersection = false
  OffsetJoinType = 0
  OffsetOpenResult = false
  PartialLoad = false
  Relative = false
  Support = -> [Array005]
  _Version = 2
FEATURE [PartDesign::Pad] Pad009
  Direction = (0,0,1)
  Length = 0.3
  Length2 = 10
  Profile = -> Binder039
  Suppressed = false
  Type = 0
FEATURE [PartDesign::SubShapeBinder] Binder040
  BindCopyOnChange = 0
  BindMode = 0
  ClaimChildren = true
  Context = -> Part010 [Body075.Binder040.]
  Fuse = false
  MakeFace = true
  OffsetFill = false
  OffsetIntersection = false
  OffsetJoinType = 0
  OffsetOpenResult = false
  PartialLoad = false
  Placement = pos=(0,382,0) rot=(0,0,1;3.14159rad)
  Relative = false
  Support = -> [Sketch066]
  _Version = 2
  expr: Support = Sketch066._self
FEATURE [PartDesign::Pocket] Pocket032
  BaseFeature = -> Pad009
  Direction = (0,0,-1)
  Length = 5
  Length2 = 5
  Midplane = true
  Profile = -> Binder040
  Suppressed = false
  Type = 1
FEATURE [Sketcher::SketchObject] Sketch098
  ArcFitTolerance = 0
  AttachmentSupport = -> [XY_Plane038]
  FullyConstrained = true
  MakeInternals = false
  MapMode = 5
  sketch-geometry (1):
    g0: Circle CenterX=0 CenterY=0 CenterZ=0 NormalX=0 NormalY=0 NormalZ=1 AngleXU=0 Radius=3.25
  constraints (2):
    c: Coincident(g0,g-1)
    c: Diameter(g0) = 6.5
FEATURE [Sketcher::SketchObject] Sketch108
  ArcFitTolerance = 0
  AttachmentSupport = -> [XY_Plane038]
  ExternalGeometry = -> [Binder039]
  FullyConstrained = true
  MakeInternals = false
  MapMode = 5
  expr: Constraints[3] = <<Properties>>.rivet_d
  sketch-geometry (2):
    g0: LineSegment [constr] StartX=112.627 StartY=65.0251 StartZ=0 EndX=101.801 EndY=58.7751 EndZ=0
    g1: Circle CenterX=101.801 CenterY=58.7751 CenterZ=0 NormalX=0 NormalY=0 NormalZ=1 AngleXU=0 Radius=1.7
  constraints (5):
    c: Coincident(g0,g-3)
    c: PointOnObject(g-1,g0)
    c: Coincident(g1,g0)
    c: Diameter(g1) = 3.4
    c: Distance(g0) = 12.5
FEATURE [PartDesign::Pocket] Pocket054
  BaseFeature = -> Pocket032
  Direction = (0,0,-1)
  Length = 5
  Length2 = 5
  Profile = -> Sketch108
  ReferenceAxis = -> Sketch108 [N_Axis]
  Reversed = true
  Suppressed = false
  Type = 0
FEATURE [PartDesign::PolarPattern] PolarPattern
  Angle = 360
  Axis = -> Z_Axis038
  BaseFeature = -> Pocket054
  Mode = 0
  Occurrences = 3
  Offset = 120
  Originals = -> [Pocket032,Pocket054]
  Suppressed = false
  TransformMode = 0
FEATURE [PartDesign::Hole] Hole015
  BaseFeature = -> PolarPattern
  CustomThreadClearance = 0
  Depth = 25
  DepthType = 0
  Diameter = 27.5
  DrillForDepth = false
  DrillPoint = 1
  DrillPointAngle = 118
  HoleCutCountersinkAngle = 90
  HoleCutCustomValues = false
  HoleCutDepth = 0
  HoleCutDiameter = 0
  HoleCutType = 0
  ModelThread = false
  Profile = -> Sketch098
  Reversed = true
  Suppressed = false
  Tapered = false
  TaperedAngle = 90
  ThreadClass = 0
  ThreadDepth = 23.5
  ThreadDepthType = 0
  ThreadDirection = 0
  ThreadFit = 0
  ThreadSize = 0
  ThreadType = 0
  Threaded = false
  UseCustomThreadClearance = false
  expr: Diameter = <<sleeve_inner_sketch>>.Constraints.outer_r * 2 + 1.5 mm
FEATURE [PartDesign::SubShapeBinder] Binder054  label="socket_fixture"
  BindCopyOnChange = 0
  BindMode = 0
  ClaimChildren = false
  Context = -> Part010 [Body075.Binder054.]
  Fuse = false
  MakeFace = true
  OffsetFill = false
  OffsetIntersection = false
  OffsetJoinType = 0
  OffsetOpenResult = false
  PartialLoad = false
  Placement = pos=(69,65,0) rot=(0,0,1;3.14159rad)
  Relative = false
  Support = -> [<external socket_fixture.FCStd>#Sketch003]
  _Version = 2
  expr: Support = socket_fixture#<<fix_holes>>._self
FEATURE [PartDesign::SubShapeBinder] Binder055  label="driver_fixture"
  BindCopyOnChange = 0
  BindMode = 0
  ClaimChildren = false
  Context = -> Part010 [Body075.Binder055.]
  Fuse = false
  MakeFace = true
  OffsetFill = false
  OffsetIntersection = false
  OffsetJoinType = 0
  OffsetOpenResult = false
  PartialLoad = false
  Placement = pos=(-24,152,0) rot=(0,0,1;0rad)
  Relative = false
  Support = -> [<external UET-VAS-060A20_12V_IP20.FCStd>#Sketch001]
  _Version = 2
  expr: Support = <<UET-VAS-060A20_12V_IP20>>#<<holes>>._self
FEATURE [PartDesign::SubShapeBinder] Binder135
  BindCopyOnChange = 0
  BindMode = 0
  ClaimChildren = false
  Context = -> Part010 [Body075.Binder135.]
  Fuse = false
  MakeFace = true
  OffsetFill = false
  OffsetIntersection = false
  OffsetJoinType = 0
  OffsetOpenResult = false
  PartialLoad = false
  Placement = pos=(35,150,0) rot=(0,0,1;0rad)
  Relative = false
  Support = -> [Sketch226]
  _Version = 2
  expr: Support = <<UV_driver_holder_holes_Sketch>>._self
FEATURE [PartDesign::Boolean] Boolean035
  BaseFeature = -> Hole015
  Group = -> [Compound084]
  Suppressed = false
  Type = 1
  UsePlacement = false
FEATURE [PartDesign::Body] Body075  label="hat_bottom_material_0.30ansi"
  AllowCompound = false
  Group = -> [Binder039,Pad009,Binder040,Pocket032,Pocket054,PolarPattern,Sketch098,Hole015,Binder054,Binder055,Sketch108,Binder135,Boolean035]
  Origin = -> Origin038
  Tip = -> Boolean035
COMPONENT P66 — recipe-attached ("hat_plexiglass_material_0.30ansi001", modeled in this document).
Construction recipe (the document's own serialized feature program — sketch geometry with constraints, then the solid features built on it; lengths are millimeters unless a unit is written):

FEATURE [PartDesign::SubShapeBinder] Binder048
  BindCopyOnChange = 0
  BindMode = 0
  ClaimChildren = true
  Context = -> Part010 [Body078.Binder048.]
  Fuse = false
  MakeFace = true
  OffsetFill = false
  OffsetIntersection = false
  OffsetJoinType = 0
  OffsetOpenResult = false
  PartialLoad = false
  Relative = false
  Support = -> [Compound043]
  _Version = 2
FEATURE [PartDesign::FeaturePython] BaseBend022  # WARN: FeaturePython — macro-defined, semantics opaque (R4)
  BendSide = 1
  BendSketch = -> Binder048
  MidPlane = false
  Reverse = false
  Suppressed = false
  length = 96
  radius = 1
  thickness = 1.5
FEATURE [PartDesign::SubShapeBinder] Binder049
  BindCopyOnChange = 0
  BindMode = 0
  ClaimChildren = true
  Context = -> Part010 [Body078.Binder049.]
  Fuse = false
  MakeFace = false
  OffsetFill = false
  OffsetIntersection = false
  OffsetJoinType = 0
  OffsetOpenResult = false
  PartialLoad = false
  Placement = pos=(0,362,6) rot=(0.57735,0.57735,0.57735;2.0944rad)
  Relative = false
  Support = -> [Sketch073]
  _Version = 2
  expr: Support = Sketch073._self
FEATURE [PartDesign::Plane] DatumPlane003
  AttachmentOffset = pos=(0,0,0) rot=(0,1,0;0.523599rad)
  AttachmentSupport = -> [XZ_Plane043]
  Length = 648.977
  MapMode = 5
  Placement = pos=(0,0,0) rot=(0.935113,0.250563,0.250563;1.63783rad)
  ResizeMode = 0
  Width = 174.677
FEATURE [PartDesign::Hole] Hole010
  BaseFeature = -> BaseBend022
  CustomThreadClearance = 0
  Depth = 1303.68
  DepthType = 1
  Diameter = 3.4
  DrillForDepth = false
  DrillPoint = 1
  DrillPointAngle = 118
  HoleCutCountersinkAngle = 90
  HoleCutCustomValues = false
  HoleCutDepth = 0
  HoleCutDiameter = 6.1
  HoleCutType = 0
  ModelThread = false
  Profile = -> Binder049
  Reversed = true
  Suppressed = false
  Tapered = false
  TaperedAngle = 90
  ThreadClass = 0
  ThreadDepth = 1303.68
  ThreadDepthType = 0
  ThreadDirection = 0
  ThreadFit = 0
  ThreadSize = 0
  ThreadType = 0
  Threaded = false
  UseCustomThreadClearance = false
  expr: Diameter = <<Properties>>.rivet_d
FEATURE [Sketcher::SketchObject] Sketch081
  ArcFitTolerance = 0
  AttachmentOffset = pos=(0,0,0) rot=(0,1,0;-1.0472rad)
  AttachmentSupport = -> [XZ_Plane043]
  FullyConstrained = true
  MakeInternals = false
  MapMode = 5
  Placement = pos=(0,0,0) rot=(-0.774597,0.447214,0.447214;4.45971rad)
  expr: Constraints[2] = <<Properties>>.rivet_d
  sketch-geometry (1):
    g0: Circle CenterX=0 CenterY=19 CenterZ=0 NormalX=0 NormalY=0 NormalZ=1 AngleXU=0 Radius=1.7
  constraints (3):
    c: PointOnObject(g0,g-2)
    c: DistanceY(g0) = 19
    c: Diameter(g0) = 3.4
FEATURE [PartDesign::Mirrored] Mirrored005
  BaseFeature = -> Hole010
  MirrorPlane = -> DatumPlane003
  Originals = -> [Hole010]
  Refine = true
  Suppressed = false
  TransformMode = 0
FEATURE [PartDesign::SubShapeBinder] Binder050
  BindCopyOnChange = 0
  BindMode = 0
  ClaimChildren = true
  Context = -> Part010 [Body078.Binder050.]
  Fuse = false
  MakeFace = true
  OffsetFill = false
  OffsetIntersection = false
  OffsetJoinType = 0
  OffsetOpenResult = false
  PartialLoad = false
  Relative = false
  Support = -> [Body075[Binder039.Array005.Compound039.Sketch068.]]
  _Version = 2
FEATURE [Sketcher::SketchObject] Sketch082
  ArcFitTolerance = 0
  AttachmentSupport = -> [XY_Plane043]
  FullyConstrained = true
  MakeInternals = false
  MapMode = 5
FEATURE [PartDesign::Pocket] Pocket117
  BaseFeature = -> Mirrored005
  Direction = (0.866025,0.5,-1e-16)
  Length = 5
  Length2 = 5
  Midplane = true
  Profile = -> Sketch081
  ReferenceAxis = -> Sketch081 [N_Axis]
  Refine = true
  Suppressed = false
  Type = 1
FEATURE [PartDesign::Body] Body078  label="hat_plexiglass_material_0.30ansi"
  AllowCompound = false
  Group = -> [Binder048,BaseBend022,Binder049,DatumPlane003,Hole010,Sketch081,Mirrored005,Binder050,Sketch082,Pocket117]
  Origin = -> Origin043
  Placement = pos=(0,0,-3) rot=(0,0,1;0rad)
  Tip = -> Pocket117
COMPONENT P67 — recipe-attached ("top_amplifier_cornrer_material_0.50ansi001", modeled in this document).
Construction recipe (the document's own serialized feature program — sketch geometry with constraints, then the solid features built on it; lengths are millimeters unless a unit is written):

FEATURE [Sketcher::SketchObject] Sketch191  label="top_corner_base_sketch"
  ArcFitTolerance = 0
  AttachmentSupport = -> [XY_Plane087]
  FullyConstrained = true
  MakeInternals = false
  MapMode = 5
  sketch-geometry (2):
    g0: LineSegment StartX=-23.3827 StartY=13.5 StartZ=0 EndX=-5.116e-13 EndY=-3.109e-13 EndZ=0
    g1: LineSegment StartX=-5.116e-13 StartY=-3.109e-13 StartZ=0 EndX=23.3827 EndY=13.5 EndZ=0
  constraints (5):
    c: Coincident(g0,g-1)
    c: Coincident(g0,g1)
    c: Symmetric(g0,g1,g-2)
    c: Angle(g1,g0) = 2.0944
    c: Distance(g1) = 27  'length'
FEATURE [PartDesign::FeaturePython] BaseBend046  # WARN: FeaturePython — macro-defined, semantics opaque (R4)
  BendSide = 0
  BendSketch = -> Sketch191
  MidPlane = false
  Reverse = false
  Suppressed = false
  length = 30
  radius = 2
  thickness = 2
FEATURE [Sketcher::SketchObject] Sketch193
  ArcFitTolerance = 0
  AttachmentOffset = pos=(0,0,0) rot=(0,1,0;0.523599rad)
  AttachmentSupport = -> [XZ_Plane087]
  FullyConstrained = true
  MakeInternals = false
  MapMode = 5
  Placement = pos=(0,0,0) rot=(0.935113,0.250563,0.250563;1.63783rad)
  expr: Constraints[6] = <<top_corner_base_sketch>>.Constraints.length
  sketch-geometry (9):
    g0: LineSegment StartX=27 StartY=20 StartZ=0 EndX=27 EndY=0 EndZ=0
    g1: LineSegment StartX=27 StartY=0 StartZ=0 EndX=4 EndY=0 EndZ=0
    g2: ArcOfCircle CenterX=24 CenterY=21.3669 CenterZ=0 NormalX=0 NormalY=0 NormalZ=1 AngleXU=0 Radius=3 StartAngle=5.42813 EndAngle=6.28319
    g3: ArcOfCircle CenterX=2.87807 CenterY=3 CenterZ=0 NormalX=0 NormalY=0 NormalZ=1 AngleXU=0 Radius=3 StartAngle=4.71239 EndAngle=5.42813
    g4: LineSegment [constr] StartX=25.9685 StartY=19.1031 StartZ=0 EndX=27 EndY=20 EndZ=0
    g5: LineSegment [constr] StartX=4 StartY=0 StartZ=0 EndX=4.84661 EndY=0.736183 EndZ=0
    g6: LineSegment StartX=4.84661 StartY=0.736183 StartZ=0 EndX=25.9685 EndY=19.1031 EndZ=0
    g7: LineSegment StartX=2.87807 StartY=0 StartZ=0 EndX=4 EndY=0 EndZ=0
    g8: LineSegment StartX=27 StartY=20 StartZ=0 EndX=27 EndY=21.3669 EndZ=0
  constraints (24):
    c: PointOnObject(g5,g-1)
    c: Coincident(g4,g0)
    c: PointOnObject(g0,g-1)
    c: Vertical(g0)
    c: Coincident(g0,g1)
    c: Coincident(g1,g5)
    c: DistanceX(g0) = 27
    c: DistanceX(g5) = 4
    c: Tangent(g2,g0)
    c: Coincident(g5,g6)
    c: Coincident(g7,g1)
    c: Horizontal(g7)
    c: Coincident(g8,g0)
    c: Coincident(g8,g2)
    c: Vertical(g8)
    c: Equal(g3,g2)
    c: Radius(g3) = 3
    c: Tangent(g3,g6) = -1.5708
    c: Tangent(g6,g2) = -1.5708
    c: Coincident(g2,g4)
    c: Parallel(g4,g6)
    c: Parallel(g5,g6)
    c: Tangent(g7,g3) = -1.5708
    c: DistanceY(g0) = 20
FEATURE [PartDesign::FeaturePython] Bend029  # WARN: FeaturePython — macro-defined, semantics opaque (R4)
  AutoMiter = true
  BaseFeature = -> BaseBend046
  BendType = 0
  LengthList = [20]
  LengthSpec = 1
  NonperforationMaxLength = 5
  Perforate = false
  PerforationAngle = 0
  PerforationInitialLength = 5
  PerforationMaxLength = 5
  ReliefFactor = 0.7
  Suppressed = false
  UseReliefFactor = false
  angle = 90
  baseObject = -> BaseBend046 [Edge17]
  bendAList = [90]
  extend1 = 0
  extend2 = 0
  gap1 = 0
  gap2 = 0
  invert = true
  kfactor = 0.5
  length = 20
  maxExtendDist = 5
  minGap = 0.1
  minReliefGap = 1
  miterangle1 = 0
  miterangle2 = 0
  offset = 0
  radius = 2
  reliefType = 0
  reliefd = 1
  reliefw = 0.8
  sketchflip = false
  sketchinvert = false
  unfold = false
  expr: radius = BaseBend046.radius
FEATURE [PartDesign::Fillet] Fillet014
  Base = -> Bend029 [Edge8,Edge40,Edge42]
  BaseFeature = -> Bend029
  Radius = 2
  SupportTransform = false
  Suppressed = false
  UseAllEdges = false
FEATURE [PartDesign::Pocket] Pocket118
  BaseFeature = -> Fillet014
  Direction = (-0.5,0.866025,-1e-16)
  Length = 5
  Length2 = 5
  Midplane = true
  Profile = -> Sketch193
  ReferenceAxis = -> Sketch193 [N_Axis]
  Suppressed = false
  Type = 1
FEATURE [PartDesign::Mirrored] Mirrored014
  BaseFeature = -> Pocket118
  MirrorPlane = -> YZ_Plane087
  Originals = -> [Pocket118]
  Suppressed = false
  TransformMode = 0
FEATURE [PartDesign::Boolean] Boolean017
  BaseFeature = -> Mirrored014
  Group = -> [Compound072]
  Refine = true
  Suppressed = false
  Type = 1
  UsePlacement = false
FEATURE [PartDesign::Body] Body113  label="top_amplifier_cornrer_material_0.50ansi"
  AllowCompound = false
  Group = -> [Sketch191,BaseBend046,Sketch193,Bend029,Fillet014,Pocket118,Mirrored014,Boolean017]
  Origin = -> Origin087
  Tip = -> Boolean017
COMPONENT P68 — recipe-attached ("sleeve_outer001", modeled in this document).
Construction recipe (the document's own serialized feature program — sketch geometry with constraints, then the solid features built on it; lengths are millimeters unless a unit is written):

FEATURE [Sketcher::SketchObject] Sketch220  label="sleeve_outer_sketch"
  ArcFitTolerance = 0
  AttachmentSupport = -> [XZ_Plane100]
  FullyConstrained = true
  MakeInternals = false
  MapMode = 5
  Placement = pos=(0,0,0) rot=(1,0,0;1.5708rad)
  expr: Constraints[13] = <<sleeve_inner_sketch>>.Constraints.outer_r + 0.25 mm
  sketch-geometry (6):
    g0: LineSegment StartX=13.25 StartY=67 StartZ=0 EndX=13.25 EndY=0 EndZ=0
    g1: LineSegment StartX=13.25 StartY=0 StartZ=0 EndX=35.25 EndY=0 EndZ=0
    g2: LineSegment StartX=35.25 StartY=0 StartZ=0 EndX=35.25 EndY=7 EndZ=0
    g3: LineSegment StartX=35.25 StartY=7 StartZ=0 EndX=20.25 EndY=7 EndZ=0
    g4: LineSegment StartX=20.25 StartY=7 StartZ=0 EndX=20.25 EndY=67 EndZ=0
    g5: LineSegment StartX=20.25 StartY=67 StartZ=0 EndX=13.25 EndY=67 EndZ=0
  constraints (20):
    c: PointOnObject(g0,g-1)
    c: Vertical(g0)
    c: Coincident(g0,g1)
    c: PointOnObject(g1,g-1)
    c: Coincident(g1,g2)
    c: Vertical(g2)
    c: Coincident(g2,g3)
    c: Horizontal(g3)
    c: Coincident(g3,g4)
    c: Vertical(g4)
    c: Coincident(g4,g5)
    c: Coincident(g5,g0)
    c: Horizontal(g5)
    c: DistanceX(g0) = 13.25
    c: DistanceX(g5,g5) = 7
    c: DistanceX(g3,g3) = 15
    c: DistanceY(g2,g2) = 7  'flange_height'
    c: DistanceY(g0,g0) = 67
    c: DistanceX(g3) = 20.25  'max_r'
    c: DistanceX(g1) = 35.25  'flange_max_r'
FEATURE [PartDesign::Revolution] Revolution001
  Angle = 360
  Angle2 = 60
  Axis = (0,2e-16,1)
  Base = (0,0,0)
  Placement = pos=(0,0,0) rot=(1,0,0;1.5708rad)
  Profile = -> Sketch220
  ReferenceAxis = -> Sketch220 [V_Axis]
  Reversed = true
  Suppressed = false
  Type = 0
FEATURE [PartDesign::Boolean] Boolean030
  BaseFeature = -> Revolution001
  Group = -> [Compound079]
  Suppressed = false
  Type = 1
  UsePlacement = false
FEATURE [PartDesign::CoordinateSystem] Local_CS039  label="sleeve_outer_flange_bottom_LCS"
  AttacherType = Attacher::AttachEngine3D
  AttachmentSupport = -> [XY_Plane100]
  MapMode = 5
FEATURE [PartDesign::CoordinateSystem] Local_CS040  label="sleeve_outer_end_LCS"
  AttacherType = Attacher::AttachEngine3D
  AttachmentOffset = pos=(0,0,67) rot=(0,0,1;0rad)
  AttachmentSupport = -> [XY_Plane100]
  MapMode = 5
  Placement = pos=(0,0,67) rot=(0,0,1;0rad)
FEATURE [PartDesign::Body] Body123  label="sleeve_outer"
  AllowCompound = false
  Group = -> [Sketch220,Revolution001,Boolean030,Local_CS039,Local_CS040]
  Origin = -> Origin100
  Tip = -> Boolean030
COMPONENT P69 — recipe-attached ("sleeve_inner001", modeled in this document).
Construction recipe (the document's own serialized feature program — sketch geometry with constraints, then the solid features built on it; lengths are millimeters unless a unit is written):

FEATURE [Sketcher::SketchObject] Sketch221  label="sleeve_inner_sketch"
  ArcFitTolerance = 0
  AttachmentSupport = -> [XZ_Plane101]
  FullyConstrained = true
  MakeInternals = false
  MapMode = 5
  Placement = pos=(0,0,0) rot=(1,0,0;1.5708rad)
  sketch-geometry (6):
    g0: LineSegment StartX=5 StartY=79 StartZ=0 EndX=5 EndY=0 EndZ=0
    g1: LineSegment StartX=5 StartY=0 StartZ=0 EndX=33 EndY=0 EndZ=0
    g2: LineSegment StartX=33 StartY=0 StartZ=0 EndX=33 EndY=8 EndZ=0
    g3: LineSegment StartX=33 StartY=8 StartZ=0 EndX=13 EndY=8 EndZ=0
    g4: LineSegment StartX=13 StartY=8 StartZ=0 EndX=13 EndY=79 EndZ=0
    g5: LineSegment StartX=13 StartY=79 StartZ=0 EndX=5 EndY=79 EndZ=0
  constraints (19):
    c: PointOnObject(g0,g-1)
    c: Vertical(g0)
    c: Coincident(g0,g1)
    c: PointOnObject(g1,g-1)
    c: Coincident(g1,g2)
    c: Vertical(g2)
    c: Coincident(g2,g3)
    c: Horizontal(g3)
    c: Coincident(g3,g4)
    c: Vertical(g4)
    c: Coincident(g4,g5)
    c: Coincident(g5,g0)
    c: Horizontal(g5)
    c: DistanceX(g0) = 5  'inner_r'
    c: DistanceX(g0,g3) = 8
    c: DistanceY(g2,g2) = 8
    c: DistanceX(g3,g3) = 20
    c: DistanceX(g3) = 13  'outer_r'
    c: DistanceY(g4,g4) = 71
FEATURE [PartDesign::Revolution] Revolution
  Angle = 360
  Angle2 = 60
  Axis = (0,2e-16,1)
  Base = (0,0,0)
  Placement = pos=(0,0,0) rot=(1,0,0;1.5708rad)
  Profile = -> Sketch221
  ReferenceAxis = -> Sketch221 [V_Axis]
  Reversed = true
  Suppressed = false
  Type = 0
FEATURE [PartDesign::Boolean] Boolean031
  BaseFeature = -> Revolution
  Group = -> [Compound083]
  Suppressed = false
  Type = 1
  UsePlacement = false
FEATURE [PartDesign::CoordinateSystem] Local_CS041  label="sleeve_inner_flange_top_LCS"
  AttacherType = Attacher::AttachEngine3D
  AttachmentOffset = pos=(0,0,8) rot=(0,0,1;0rad)
  AttachmentSupport = -> [XY_Plane101]
  MapMode = 5
  Placement = pos=(0,0,8) rot=(0,0,1;0rad)
FEATURE [PartDesign::CoordinateSystem] Local_CS042  label="sleeve_inner_end_LCS"
  AttacherType = Attacher::AttachEngine3D
  AttachmentOffset = pos=(0,0,79) rot=(0,0,1;0rad)
  AttachmentSupport = -> [XY_Plane101]
  MapMode = 5
  Placement = pos=(0,0,79) rot=(0,0,1;0rad)
FEATURE [PartDesign::Body] Body124  label="sleeve_inner"
  AllowCompound = false
  Group = -> [Sketch221,Revolution,Boolean031,Local_CS041,Local_CS042]
  Origin = -> Origin101
  Tip = -> Boolean031
COMPONENT P70 — geometry summary ("led_holder_fix_extrude001"; no construction recipe available for this part):
  bounding box: 1096.4 x 10.0 x 3.4 mm
  tessellated surface: 300 triangles
  volume: 454 mm^3 (1% of its bounding box)
  symmetry: 2-fold rotationally symmetric about the x axis; 2-fold rotationally symmetric about the y axis; revolution-symmetric about the z axis through its bounding-box center; mirror-symmetric across its x mid-plane, y mid-plane, z mid-plane
COMPONENT P71 — geometry summary ("pillar3_pillar3_dec_corner_common001"; no construction recipe available for this part):
  bounding box: 1187.4 x 57.6 x 25.7 mm
  tessellated surface: 1,508 triangles
  volume: 4069 mm^3 (0% of its bounding box)
  symmetry: mirror-symmetric across its x mid-plane
COMPONENT P72 — same part as P37; its construction recipe is shown at P37.
COMPONENT P73 — recipe-attached ("sink", modeled in this document).
Construction recipe (the document's own serialized feature program — sketch geometry with constraints, then the solid features built on it; lengths are millimeters unless a unit is written):

FEATURE [Sketcher::SketchObject] Sketch037
  ArcFitTolerance = 0
  AttachmentSupport = -> [XY_Plane028]
  FullyConstrained = false
  MakeInternals = false
  MapMode = 5
  sketch-geometry (2):
    g0: LineSegment StartX=0 StartY=0 StartZ=0 EndX=74.4649 EndY=59.2839 EndZ=0
    g1: LineSegment StartX=0 StartY=0 StartZ=0 EndX=-93.8109 EndY=73.3435 EndZ=0
  constraints (2):
    c: Coincident(g0,g-1)
    c: Coincident(g1,g0)
FEATURE [Part::Part2DObjectPython] Line  label="sink_bend_line"  # Draft 2D object (typed FeaturePython)
  Area = 0
  AttachmentOffset = pos=(304.73,175.936,20) rot=(0,0,1;0rad)
  AttachmentSupport = -> [XY_Plane028]
  BendAngle = 6.48542
  ChamferSize = 0
  Closed = false
  End = (0,0,0)
  FaceAngle = 3.2479
  FilletRadius = 0
  Length = 352.44
  MakeFace = true
  MapMode = 5
  Placement = pos=(304.73,175.936,20) rot=(0,0,1;0rad)
  Points = (2) [(0,0,0),(-304.73,-175.936,-20)]
  Start = (304.73,175.936,20)
  Subdivisions = 0
  expr: .AttachmentOffset.Base.x = Spreadsheet.total_length * cos(30)
  expr: .AttachmentOffset.Base.y = Spreadsheet.total_length * sin(30)
  expr: BendAngle = atan2(.AttachmentOffset.Base.z; .AttachmentOffset.Base.y)
  expr: End = tuple(0; 0; 0)
  expr: FaceAngle = atan2(.AttachmentOffset.Base.z; Length)
FEATURE [PartDesign::Line] DatumLine
  AttacherType = Attacher::AttachEngineLine
  AttachmentSupport = -> [Z_Axis028]
  Length = 20
  MapMode = 29
  ResizeMode = 0
FEATURE [PartDesign::Line] DatumLine001
  AttacherType = Attacher::AttachEngineLine
  AttachmentSupport = -> [Line,X_Axis028]
  Length = 20
  MapMode = 24
  Placement = pos=(304.73,175.936,20) rot=(0.57735,-0.57735,-0.57735;2.0944rad)
  ResizeMode = 0
FEATURE [Sketcher::SketchObject] Sketch038
  ArcFitTolerance = 0
  AttachmentSupport = -> [Line]
  ExternalGeometry = -> [DatumLine001]
  FullyConstrained = false
  MakeInternals = false
  MapMode = 45
  Placement = pos=(152.365,87.9679,10) rot=(0.368581,0.6384,0.675717;2.39766rad)
  sketch-geometry (3):
    g0: LineSegment StartX=4.75e-14 StartY=4.27e-14 StartZ=0 EndX=4.75e-14 EndY=93.8582 EndZ=0
    g1: LineSegment StartX=4.75e-14 StartY=4.27e-14 StartZ=0 EndX=35.2298 EndY=3.46271 EndZ=0
    g2: ArcOfCircle CenterX=2.5 CenterY=2.75777 CenterZ=0 NormalX=0 NormalY=0 NormalZ=1 AngleXU=0 Radius=2.5 StartAngle=3.14159 EndAngle=4.81036
  constraints (9):
    c: Coincident(g0,g-1)
    c: Vertical(g0)
    c: Coincident(g1,g0)
    c: PointOnObject(g1,g-3)
    c: Angle(g-3) = 0.0979746
    c: Angle(g1,g0) = 1.47282  'bend_angle'
    c: Tangent(g2,g0) = 1.5708
    c: Tangent(g2,g1) = -1.5708
    c: Radius(g2) = 2.5
FEATURE [PartDesign::CoordinateSystem] Local_CS
  AttacherType = Attacher::AttachEngine3D
  AttachmentOffset = pos=(0,0,0) rot=(1,0,0;0.113192rad)
  AttachmentSupport = -> [XY_Plane028]
  MapMode = 5
  Placement = pos=(0,0,0) rot=(1,0,0;0.113192rad)
  expr: .AttachmentOffset.Rotation.Angle = Line.BendAngle
FEATURE [Sketcher::SketchObject] Sketch039
  ArcFitTolerance = 0
  AttachmentSupport = -> [Local_CS]
  ExternalGeometry = -> [Line,Sketch038]
  FullyConstrained = true
  MakeInternals = false
  MapMode = 5
  Placement = pos=(0,0,0) rot=(1,0,0;0.113192rad)
  sketch-geometry (3):
    g0: LineSegment StartX=2e-16 StartY=3.18954 StartZ=0 EndX=-459.172 EndY=270 EndZ=0
    g1: LineSegment StartX=2e-16 StartY=3.18954 StartZ=0 EndX=459.172 EndY=270 EndZ=0
    g2: LineSegment StartX=459.172 StartY=270 StartZ=0 EndX=-459.172 EndY=270 EndZ=0
  constraints (8):
    c: Coincident(g2,g1)
    c: DistanceY(g1) = 270
    c: Coincident(g0,g2)
    c: Symmetric(g1,g0,g-2)
    c: Coincident(g1,g0)
    c: PointOnObject(g0,g-2)
    c: Parallel(g1,g-3)
    c: PointOnObject(g-4,g1)
FEATURE [PartDesign::FeaturePython] BaseBend011  # WARN: FeaturePython — macro-defined, semantics opaque (R4)
  BendSide = 0
  BendSketch = -> Sketch039
  MidPlane = false
  Reverse = false
  Suppressed = false
  length = 100
  radius = 2
  thickness = 0.5
FEATURE [PartDesign::FeaturePython] Bend004  # WARN: FeaturePython — macro-defined, semantics opaque (R4)
  AutoMiter = false
  BaseFeature = -> BaseBend011
  BendType = 0
  LengthList = [100]
  LengthSpec = 1
  NonperforationMaxLength = 5
  Perforate = false
  PerforationAngle = 0
  PerforationInitialLength = 5
  PerforationMaxLength = 5
  ReliefFactor = 0.7
  Suppressed = false
  UseReliefFactor = false
  angle = 95.6135
  baseObject = -> BaseBend011 [Edge3,Edge8]
  bendAList = [95.6135]
  extend1 = 2
  extend2 = 0
  gap1 = 0
  gap2 = 0
  invert = true
  kfactor = 0.5
  length = 100
  maxExtendDist = 5
  minGap = 0.1
  minReliefGap = 1
  miterangle1 = 0
  miterangle2 = 0
  offset = 0
  radius = 2
  reliefType = 0
  reliefd = 1
  reliefw = 0.8
  sketchflip = false
  sketchinvert = false
  unfold = false
  expr: angle = 180 deg - Sketch038.Constraints.bend_angle
  expr: radius = BaseBend011.radius
FEATURE [Sketcher::SketchObject] Sketch040
  ArcFitTolerance = 0
  AttachmentSupport = -> [Local_CS]
  ExternalGeometry = -> [Line,Sketch038]
  FullyConstrained = true
  MakeInternals = false
  MapMode = 5
  Placement = pos=(0,0,0) rot=(1,0,0;0.113192rad)
  sketch-geometry (13):
    g0: ArcOfCircle CenterX=0 CenterY=-630 CenterZ=0 NormalX=0 NormalY=0 NormalZ=1 AngleXU=0 Radius=870 StartAngle=1.24863 EndAngle=1.89296
    g1: LineSegment [constr] StartX=0 StartY=0 StartZ=0 EndX=294.959 EndY=171.391 EndZ=0
    g2: LineSegment [constr] StartX=150.979 StartY=90.9189 StartZ=0 EndX=293.573 EndY=173.776 EndZ=0
    g3: LineSegment [constr] StartX=-294.959 StartY=171.391 StartZ=0 EndX=0 EndY=0 EndZ=0
    g4: LineSegment StartX=-294.959 StartY=171.391 StartZ=0 EndX=-464.661 EndY=270 EndZ=0
    g5: LineSegment StartX=-464.661 StartY=270 StartZ=0 EndX=464.661 EndY=270 EndZ=0
    g6: LineSegment StartX=464.661 StartY=270 StartZ=0 EndX=294.959 EndY=171.391 EndZ=0
    g7: LineSegment StartX=294.959 StartY=171.391 StartZ=0 EndX=294.075 EndY=172.911 EndZ=0
    g8: LineSegment StartX=294.075 StartY=172.911 StartZ=0 EndX=293.573 EndY=173.776 EndZ=0
    g9: LineSegment [constr] StartX=-294.959 StartY=171.391 StartZ=0 EndX=-294.959 EndY=171.391 EndZ=0
    g10: LineSegment StartX=293.573 StartY=173.776 StartZ=0 EndX=275.46 EndY=195.241 EndZ=0
    g11: LineSegment StartX=-293.573 StartY=173.776 StartZ=0 EndX=-275.46 EndY=195.241 EndZ=0
    g12: LineSegment StartX=-294.959 StartY=171.391 StartZ=0 EndX=-293.573 EndY=173.776 EndZ=0
  constraints (34):
    c: Coincident(g1,g-1)
    c: PointOnObject(g1,g-3)
    c: Coincident(g7,g1)
    c: Distance(g1) = 341.139
    c: Coincident(g2,g-4)
    c: Parallel(g2,g1)
    c: DistanceY(g0) = -630
    c: Radius(g0) = 870
    c: Coincident(g9,g3)
    c: Coincident(g3,g1)
    c: Symmetric(g9,g7,g-2)
    c: Coincident(g4,g5)
    c: Coincident(g5,g6)
    c: Parallel(g6,g2)
    c: Symmetric(g5,g4,g-2)
    c: DistanceY(g5) = 270
    c: Coincident(g2,g8)
    c: Coincident(g7,g8)
    c: Perpendicular(g1,g7)
    c: Perpendicular(g1,g8)
    c: Distance(g8) = 1
    c: Coincident(g10,g0)
    c: Coincident(g11,g0)
    c: PointOnObject(g0,g-2)
    c: Coincident(g10,g8)
    c: Coincident(g12,g9)
    c: Coincident(g4,g12)
    c: Coincident(g12,g11)
    c: Symmetric(g4,g6,g-2)
    c: Symmetric(g8,g11,g-2)
    c: Horizontal(g0,g0)
    c: Distance(g10) = 28.0862
    c: Angle(g10,g2) = 1.39626
    c: Coincident(g6,g7)
FEATURE [PartDesign::SubShapeBinder] Binder031
  BindCopyOnChange = 0
  BindMode = 0
  ClaimChildren = false
  Context = -> Part007 [Body020.Binder031.]
  Fuse = false
  MakeFace = true
  OffsetFill = false
  OffsetIntersection = false
  OffsetJoinType = 0
  OffsetOpenResult = false
  PartialLoad = false
  Relative = true
  _Version = 2
FEATURE [PartDesign::Pocket] Pocket022
  BaseFeature = -> Bend004
  Direction = (0,0.11295,-0.993601)
  Length = 2.5
  Length2 = 5
  Profile = -> Sketch040
  ReferenceAxis = -> Sketch040 [N_Axis]
  Refine = true
  Reversed = true
  Suppressed = false
  Type = 0
FEATURE [Sketcher::SketchObject] Sketch042
  ArcFitTolerance = 0
  AttachmentSupport = -> [XY_Plane028]
  FullyConstrained = true
  MakeInternals = false
  MapMode = 5
  sketch-geometry (7):
    g0: LineSegment StartX=-18.3205 StartY=-10 StartZ=0 EndX=-0.5 EndY=0.288675 EndZ=0
    g1: LineSegment StartX=18.3205 StartY=-10 StartZ=0 EndX=-18.3205 EndY=-10 EndZ=0
    g2: LineSegment [constr] StartX=1 StartY=1.5e-15 StartZ=0 EndX=-1e-16 EndY=0.57735 EndZ=0
    g3: LineSegment [constr] StartX=1.3e-15 StartY=-2.2e-15 StartZ=0 EndX=0.5 EndY=0.288675 EndZ=0
    g4: LineSegment StartX=0.5 StartY=0.288675 StartZ=0 EndX=18.3205 EndY=-10 EndZ=0
    g5: LineSegment StartX=-2.6e-15 StartY=1.1547 StartZ=0 EndX=0.5 EndY=0.288675 EndZ=0
    g6: LineSegment StartX=-0.5 StartY=0.288675 StartZ=0 EndX=-2.6e-15 EndY=1.1547 EndZ=0
  constraints (19):
    c: Coincident(g4,g1)
    c: Coincident(g1,g0)
    c: Symmetric(g4,g0,g-2)
    c: PointOnObject(g2,g-1)
    c: PointOnObject(g2,g-2)
    c: Angle(g2) = 2.61799
    c: Distance(g-1,g2) = 0.5
    c: Coincident(g3,g-1)
    c: PointOnObject(g3,g2)
    c: Angle(g3) = 0.523599
    c: PointOnObject(g2,g4)
    c: Perpendicular(g3,g5)
    c: Coincident(g4,g5)
    c: Coincident(g4,g3)
    c: PointOnObject(g5,g-2)
    c: Coincident(g6,g0)
    c: Coincident(g6,g5)
    c: Symmetric(g4,g0,g-2)
    c: DistanceY(g1) = -10
FEATURE [Sketcher::SketchObject] Sketch041
  ArcFitTolerance = 0
  AttachmentOffset = pos=(0,0,0) rot=(0,1,0;0.523599rad)
  AttachmentSupport = -> [XZ_Plane028]
  ExternalGeometry = -> [Sketch038,Sketch042,Sketch040]
  FullyConstrained = false
  MakeInternals = false
  MapMode = 5
  Placement = pos=(0,0,0) rot=(0.935113,0.250563,0.250563;1.63783rad)
  sketch-geometry (16):
    g0: LineSegment StartX=340.573 StartY=19.628 StartZ=0 EndX=340.432 EndY=22.112 EndZ=0
    g1: LineSegment [constr] StartX=175.779 StartY=12.7533 StartZ=0 EndX=340.432 EndY=22.112 EndZ=0
    g2: LineSegment StartX=0.57735 StartY=196.491 StartZ=0 EndX=638.392 EndY=196.491 EndZ=0
    g3: LineSegment StartX=638.392 StartY=196.491 StartZ=0 EndX=638.392 EndY=36.5557 EndZ=0
    g4: LineSegment StartX=638.392 StartY=36.5557 StartZ=0 EndX=340.573 EndY=19.628 EndZ=0
    g5: LineSegment StartX=340.432 StartY=22.112 StartZ=0 EndX=340.432 EndY=85 EndZ=0
    g6: LineSegment StartX=0.57735 StartY=85 StartZ=0 EndX=0.57735 EndY=196.491 EndZ=0
    g7: LineSegment StartX=335.432 StartY=90 StartZ=0 EndX=5.57735 EndY=90 EndZ=0
    g8: ArcOfCircle CenterX=5.57735 CenterY=85 CenterZ=0 NormalX=0 NormalY=0 NormalZ=1 AngleXU=0 Radius=5 StartAngle=1.5708 EndAngle=3.14159
    g9: ArcOfCircle CenterX=335.432 CenterY=85 CenterZ=0 NormalX=0 NormalY=0 NormalZ=1 AngleXU=0 Radius=5 StartAngle=2e-16 EndAngle=1.5708
    g10: GeomPoint [constr] X=340.432 Y=90 Z=0
    g11: LineSegment StartX=0.57735 StartY=0 StartZ=0 EndX=0.57735 EndY=27.6603 EndZ=0
    g12: ArcOfCircle CenterX=5 CenterY=27.6603 CenterZ=0 NormalX=0 NormalY=0 NormalZ=1 AngleXU=0 Radius=4.42265 StartAngle=3.14159 EndAngle=4.18879
    g13: ArcOfCircle CenterX=0.57735 CenterY=20 CenterZ=0 NormalX=0 NormalY=0 NormalZ=1 AngleXU=0 Radius=4.42265 StartAngle=-2.31e-14 EndAngle=1.0472
    g14: LineSegment StartX=5 StartY=20 StartZ=0 EndX=5 EndY=0 EndZ=0
    g15: LineSegment StartX=5 StartY=0 StartZ=0 EndX=0.57735 EndY=0 EndZ=0
  constraints (39):
    c: Coincident(g1,g-3)
    c: Coincident(g1,g0)
    c: Perpendicular(g-3,g1)
    c: Perpendicular(g1,g0)
    c: Coincident(g5,g0)
    c: Coincident(g6,g2)
    c: Horizontal(g2)
    c: Coincident(g2,g3)
    c: Vertical(g3)
    c: Coincident(g3,g4)
    c: Coincident(g4,g0)
    c: Parallel(g4,g1)
    c: Vertical(g5)
    c: Vertical(g6)
    c: Vertical(g6,g-4)
    c: Horizontal(g7)
    c: Tangent(g8,g7) = -1.5708
    c: Tangent(g8,g6) = 1.5708
    c: PointOnObject(g10,g5)
    c: PointOnObject(g10,g7)
    c: Tangent(g5,g9) = -1.5708
    c: Tangent(g7,g9) = -1.5708
    c: Equal(g9,g8)
    c: Coincident(g11,g-4)
    c: Vertical(g11)
    c: PointOnObject(g13,g11)
    c: PointOnObject(g14,g-1)
    c: Vertical(g14)
    c: Coincident(g15,g14)
    c: Coincident(g15,g11)
    c: Tangent(g13,g12) = 1.5708
    c: Tangent(g12,g11) = 1.5708
    c: Tangent(g14,g13) = 1.5708
    c: Equal(g13,g12)
    c: DistanceX(g14) = 5
    c: DistanceY(g13) = 20
    c: DistanceY(g7) = 90
    c: Radius(g9) = 5
    c: Coincident(g0,g-5)
FEATURE [Sketcher::SketchObject] Sketch043
  ArcFitTolerance = 0
  AttachmentSupport = -> [Local_CS]
  FullyConstrained = false
  MakeInternals = false
  MapMode = 5
  Placement = pos=(0,0,0) rot=(1,0,0;0.113192rad)
  expr: Constraints[12] = Sketch038.Constraints.bend_angle / 2
  sketch-geometry (7):
    g0: ArcOfCircle CenterX=-2.2e-14 CenterY=1.72e-14 CenterZ=0 NormalX=0 NormalY=0 NormalZ=1 AngleXU=0 Radius=19.4106 StartAngle=5.52221 EndAngle=10.1858
    g1: ArcOfCircle CenterX=17.4885 CenterY=-16.6545 CenterZ=0 NormalX=0 NormalY=0 NormalZ=1 AngleXU=0 Radius=4.73935 StartAngle=2.38062 EndAngle=3.72466
    g2: ArcOfCircle CenterX=-17.4885 CenterY=-16.6545 CenterZ=0 NormalX=0 NormalY=0 NormalZ=1 AngleXU=0 Radius=4.73935 StartAngle=5.70012 EndAngle=7.04416
    g3: LineSegment StartX=13.5322 StartY=-19.2639 StartZ=0 EndX=49.1398 EndY=-73.2508 EndZ=0
    g4: LineSegment StartX=-13.5322 StartY=-19.2639 StartZ=0 EndX=-49.1398 EndY=-73.2508 EndZ=0
    g5: LineSegment StartX=-49.1398 StartY=-73.2508 StartZ=0 EndX=49.1398 EndY=-73.2508 EndZ=0
    g6: LineSegment StartX=-86.3387 StartY=-141.994 StartZ=0 EndX=130.665 EndY=54.7259 EndZ=0
  constraints (13):
    c: Coincident(g0,g-1)
    c: Coincident(g5,g4)
    c: Coincident(g5,g3)
    c: Tangent(g3,g1) = -1.5708
    c: Tangent(g1,g0) = 1.5708
    c: Tangent(g2,g0) = 1.5708
    c: Tangent(g4,g2) = 1.5708
    c: Symmetric(g4,g3,g-2)
    c: Symmetric(g2,g1,g-2)
    c: DistanceX(g1) = 13.5322
    c: DistanceY(g1) = -19.2639
    c: Angle(g3) = -0.987729
    c: Angle(g6) = 0.736411
FEATURE [Sketcher::SketchObject] Sketch064
  ArcFitTolerance = 0
  AttachmentSupport = -> [Local_CS]
  FullyConstrained = true
  MakeInternals = false
  MapMode = 5
  Placement = pos=(0,0,0) rot=(1,0,0;0.113192rad)
  expr: Constraints[3] = <<Properties>>.rivet_d
  sketch-geometry (4):
    g0: Circle CenterX=-88.3 CenterY=228.865 CenterZ=0 NormalX=0 NormalY=0 NormalZ=1 AngleXU=0 Radius=1.7
    g1: Circle CenterX=88.3 CenterY=228.865 CenterZ=0 NormalX=0 NormalY=0 NormalZ=1 AngleXU=0 Radius=1.7
    g2: Circle CenterX=261.291 CenterY=193.3 CenterZ=0 NormalX=0 NormalY=0 NormalZ=1 AngleXU=0 Radius=1.7
    g3: Circle CenterX=-261.291 CenterY=193.3 CenterZ=0 NormalX=0 NormalY=0 NormalZ=1 AngleXU=0 Radius=1.7
  constraints (10):
    c: Equal(g2,g1)
    c: Equal(g2,g0)
    c: Equal(g2,g3)
    c: Diameter(g2) = 3.4
    c: DistanceX(g1) = 88.3
    c: DistanceY(g1) = 228.865
    c: DistanceX(g2) = 261.291
    c: DistanceY(g2) = 193.3
    c: Symmetric(g0,g1,g-2)
    c: Symmetric(g3,g2,g-2)
FEATURE [PartDesign::SubShapeBinder] Binder061
  BindCopyOnChange = 0
  BindMode = 0
  ClaimChildren = false
  Context = -> Part007 [Body021.Binder061.]
  Fuse = false
  MakeFace = true
  OffsetFill = false
  OffsetIntersection = false
  OffsetJoinType = 0
  OffsetOpenResult = false
  PartialLoad = false
  Relative = false
  Support = -> [Body020[Pocket022.Sketch040.]]
  _Version = 2
FEATURE [PartDesign::SubShapeBinder] Binder062
  BindCopyOnChange = 0
  BindMode = 0
  ClaimChildren = false
  Context = -> Part007 [Body021.Binder062.]
  Fuse = false
  MakeFace = true
  OffsetFill = false
  OffsetIntersection = false
  OffsetJoinType = 0
  OffsetOpenResult = false
  PartialLoad = false
  Relative = false
  Support = -> [Body020[Pocket029.Sketch064.]]
  _Version = 2
FEATURE [Sketcher::SketchObject] Sketch109
  ArcFitTolerance = 0
  AttachmentSupport = -> [XY_Plane029]
  ExternalGeometry = -> [Binder061]
  FullyConstrained = false
  MakeInternals = false
  MapMode = 5
  sketch-geometry (19):
    g0: ArcOfCircle CenterX=291.996 CenterY=172.865 CenterZ=0 NormalX=0 NormalY=0 NormalZ=1 AngleXU=0 Radius=1 StartAngle=5.23599 EndAngle=6.98132
    g1: LineSegment StartX=5.51e-14 StartY=239 StartZ=0 EndX=5.51e-14 EndY=240 EndZ=0
    g2: LineSegment StartX=292.496 StartY=171.999 StartZ=0 EndX=287.719 EndY=169.241 EndZ=0
    g3: ArcOfCircle CenterX=287.219 CenterY=170.107 CenterZ=0 NormalX=0 NormalY=0 NormalZ=1 AngleXU=0 Radius=1 StartAngle=3.90153 EndAngle=5.23599
    g4: LineSegment StartX=5.51e-14 StartY=239 StartZ=0 EndX=5.51e-14 EndY=224 EndZ=0
    g5: ArcOfCircle CenterX=243.002 CenterY=128.086 CenterZ=0 NormalX=0 NormalY=0 NormalZ=1 AngleXU=0 Radius=60 StartAngle=0.759936 EndAngle=1.27733
    g6: GeomPoint [constr] X=287.033 Y=168.845 Z=0
    g7: GeomPoint [constr] X=293.528 Y=172.595 Z=0
    g8: ArcOfCircle CenterX=1.26657 CenterY=-621.999 CenterZ=0 NormalX=0 NormalY=0 NormalZ=1 AngleXU=0 Radius=862 StartAngle=1.25533 EndAngle=1.57227
    g9: LineSegment [constr] StartX=5.28e-14 StartY=220.8 StartZ=0 EndX=5.51e-14 EndY=240 EndZ=0
    g10: ArcOfCircle [constr] CenterX=0 CenterY=-641.2 CenterZ=0 NormalX=0 NormalY=0 NormalZ=1 AngleXU=0 Radius=862 StartAngle=1.25386 EndAngle=1.5708
    g11: LineSegment [constr] StartX=5.51e-14 StartY=240 StartZ=0 EndX=268.713 EndY=197.462 EndZ=0
    g12: LineSegment [constr] StartX=5.28e-14 StartY=220.8 StartZ=0 EndX=268.65 EndY=177.867 EndZ=0
    g13: ArcOfCircle CenterX=0 CenterY=-676.059 CenterZ=0 NormalX=0 NormalY=0 NormalZ=1 AngleXU=0 Radius=900.059 StartAngle=1.27733 EndAngle=1.5708
    g14: Circle [constr] CenterX=268.65 CenterY=177.867 CenterZ=0 NormalX=0 NormalY=0 NormalZ=1 AngleXU=0 Radius=4
    g15: LineSegment [constr] StartX=0 StartY=0 StartZ=0 EndX=301.632 EndY=174.148 EndZ=0
    g16: LineSegment [constr] StartX=0 StartY=0 StartZ=0 EndX=-15 EndY=25.9808 EndZ=0
    g17: ArcOfCircle CenterX=262.507 CenterY=178.449 CenterZ=0 NormalX=0 NormalY=0 NormalZ=1 AngleXU=0 Radius=20 StartAngle=0.698132 EndAngle=1.25533
    g18: LineSegment StartX=292.762 StartY=173.508 StartZ=0 EndX=277.828 EndY=191.305 EndZ=0
  constraints (51):
    c: Tangent(g17,g8) = -1.5708
    c: Vertical(g1)
    c: PointOnObject(g1,g-2)
    c: Angle(g2) = -2.61799
    c: Tangent(g2,g0) = 1.5708
    c: DistanceY(g1,g1) = 1
    c: Tangent(g3,g2) = 1.5708
    c: Radius(g3) = 1
    c: Equal(g3,g0)
    c: Coincident(g4,g1)
    c: Vertical(g4)
    c: Distance(g4) = 15
    c: Tangent(g5,g3) = 1.5708
    c: PointOnObject(g7,g2)
    c: PointOnObject(g6,g2)
    c: PointOnObject(g6,g5)
    c: Coincident(g8,g1)
    c: PointOnObject(g9,g-2)
    c: DistanceY(g9,g4) = 3.2
    c: Coincident(g9,g1)
    c: Radius(g8) = 862  'outer_r'
    c: Distance(g6,g7) = 7.5
    c: PointOnObject(g10,g-2)
    c: Coincident(g11,g1)
    c: Coincident(g11,g17)
    c: Coincident(g12,g10)
    c: Coincident(g12,g10)
    c: Equal(g10,g8)
    c: Equal(g12,g11)
    c: Coincident(g10,g9)
    c: PointOnObject(g13,g-2)
    c: Coincident(g13,g4)
    c: Tangent(g13,g5) = -1.5708
    c: Coincident(g14,g10)
    c: Tangent(g14,g5)
    c: Radius(g14) = 4
    c: Coincident(g15,g-1)
    c: Angle(g15) = 0.523599
    c: Distance(g6,g15) = 2.7076
    c: DistanceY(g1) = 240
    c: Coincident(g16,g15)
    c: Perpendicular(g15,g16)
    c: Distance(g7,g16) = 340.5
    c: Tangent(g18,g0) = -1.5708
    c: Angle(g18) = 2.26893
    c: Tangent(g17,g18) = -1.5708
    c: PointOnObject(g8,g-5)
    c: Radius(g17) = 20
    c: PointOnObject(g7,g18)
    c: Radius(g5) = 60
    c: Distance(g16) = 30
FEATURE [PartDesign::Pad] Pad014
  Direction = (0,0,1)
  Length = 3
  Length2 = 10
  Profile = -> Sketch109
  ReferenceAxis = -> Sketch109 [N_Axis]
  Suppressed = false
  Type = 0
FEATURE [PartDesign::Mirrored] Mirrored008
  BaseFeature = -> Pad014
  MirrorPlane = -> Sketch109 [V_Axis]
  Originals = -> [Pad014]
  Refine = true
  Suppressed = false
  TransformMode = 0
FEATURE [PartDesign::Pocket] Pocket055
  BaseFeature = -> Mirrored008
  Direction = (0,0,-1)
  Length = 5
  Length2 = 5
  Profile = -> Binder062
  Reversed = true
  Suppressed = false
  Type = 0
FEATURE [PartDesign::Body] Body021
  AllowCompound = false
  Group = -> [Binder061,Binder062,Sketch109,Pad014,Mirrored008,Pocket055]
  Origin = -> Origin029
  Placement = pos=(0,0,0) rot=(1,0,0;0.116239rad)
  Tip = -> Pocket055
FEATURE [Sketcher::SketchObject] Sketch219
  ArcFitTolerance = 0
  FullyConstrained = false
  MakeInternals = false
  MapMode = 5
  Placement = pos=(0,8e-15,-6.7e-14) rot=(1,0,0;3.25479rad)
  sketch-geometry (6):
    g0: LineSegment StartX=297.803 StartY=-177.345 StartZ=0 EndX=303.917 EndY=-182.504 EndZ=0
    g1: LineSegment StartX=303.917 StartY=-182.504 StartZ=0 EndX=285.803 EndY=-203.969 EndZ=0
    g2: LineSegment StartX=285.803 StartY=-203.969 StartZ=0 EndX=276.608 EndY=-196.209 EndZ=0
    g3: LineSegment StartX=279.192 StartY=-196.205 StartZ=0 EndX=297.807 EndY=-180.398 EndZ=0
    g4: ArcOfCircle CenterX=296.513 CenterY=-178.873 CenterZ=0 NormalX=0 NormalY=0 NormalZ=1 AngleXU=0 Radius=2 StartAngle=5.41641 EndAngle=7.15307
    g5: ArcOfCircle CenterX=277.898 CenterY=-194.681 CenterZ=0 NormalX=0 NormalY=0 NormalZ=1 AngleXU=0 Radius=2 StartAngle=4.01147 EndAngle=5.41641
  constraints (13):
    c: Coincident(g0,g1)
    c: Coincident(g1,g2)
    c: Perpendicular(g1,g2)
    c: Perpendicular(g0,g1)
    c: Tangent(g4,g0) = 1.5708
    c: Tangent(g5,g2) = 1.5708
    c: Tangent(g5,g3) = -1.5708
    c: Tangent(g4,g3) = -1.5708
    c: Equal(g4,g5)
    c: Radius(g4) = 2
    c: Distance(g0) = 8
    c: Distance(g2) = 12.0319
    c: Distance(g3,g1) = 10.0593
FEATURE [PartDesign::FeaturePython] Bend033  # WARN: FeaturePython — macro-defined, semantics opaque (R4)
  AutoMiter = true
  BaseFeature = -> Pocket022
  BendType = 0
  LengthList = [10]
  LengthSpec = 0
  NonperforationMaxLength = 5
  Perforate = false
  PerforationAngle = 0
  PerforationInitialLength = 5
  PerforationMaxLength = 5
  ReliefFactor = 0.7
  Suppressed = false
  UseReliefFactor = false
  angle = 90
  baseObject = -> Pocket022 [Edge64,Edge69]
  bendAList = [90]
  extend1 = 0
  extend2 = 0
  gap1 = 0
  gap2 = 0
  invert = false
  kfactor = 0.5
  length = 10
  maxExtendDist = 5
  minGap = 0.2
  minReliefGap = 1
  miterangle1 = 0
  miterangle2 = 0
  offset = 0
  radius = 2
  reliefType = 0
  reliefd = 1
  reliefw = 0.8
  sketchflip = false
  sketchinvert = false
  unfold = true
  expr: radius = BaseBend011.radius
FEATURE [PartDesign::Pocket] Pocket131
  BaseFeature = -> Bend033
  Direction = (0,-0.11295,0.993601)
  Length = 5
  Length2 = 5
  Profile = -> Sketch219
  ReferenceAxis = -> Sketch219 [N_Axis]
  Suppressed = false
  Type = 0
FEATURE [PartDesign::Mirrored] Mirrored017
  BaseFeature = -> Pocket131
  MirrorPlane = -> YZ_Plane028
  Originals = -> [Pocket131]
  Suppressed = false
  TransformMode = 0
FEATURE [PartDesign::Pocket] Pocket024
  BaseFeature = -> Mirrored017
  Direction = (0,0,-1)
  Length = 5
  Length2 = 5
  Midplane = true
  Profile = -> Sketch042
  ReferenceAxis = -> Sketch042 [N_Axis]
  Suppressed = false
  Type = 1
FEATURE [PartDesign::FeaturePython] CornerRelief  # WARN: FeaturePython — macro-defined, semantics opaque (R4)
  BaseFeature = -> Pocket024
  ReliefSketch = 0
  Size = 6
  SizeRatio = 1.5
  Sketch = -> Sketch043
  Suppressed = false
  XOffset = 0
  YOffset = 0
  baseObject = -> Pocket024 [Edge35,Edge16]
  kfactor = 0.5
FEATURE [PartDesign::Pocket] Pocket023
  BaseFeature = -> CornerRelief
  Direction = (-0.5,0.866025,-1e-16)
  Length = 0.6
  Length2 = 5
  Profile = -> Sketch041
  ReferenceAxis = -> Sketch041 [N_Axis]
  Suppressed = false
  Type = 0
FEATURE [PartDesign::Mirrored] Mirrored002
  BaseFeature = -> Pocket023
  MirrorPlane = -> YZ_Plane028
  Originals = -> [Pocket023]
  Refine = true
  Suppressed = false
  TransformMode = 0
FEATURE [PartDesign::Boolean] Boolean008
  BaseFeature = -> Mirrored002
  Group = -> [Compound028]
  Suppressed = false
  Type = 1
  UsePlacement = false
  expr: Group = <<sink_fix001>>._self
FEATURE [PartDesign::Pocket] Pocket029
  BaseFeature = -> Boolean008
  Direction = (0,0.11295,-0.993601)
  Length = 5
  Length2 = 5
  Profile = -> Sketch064
  ReferenceAxis = -> Sketch064 [N_Axis]
  Reversed = true
  Suppressed = false
  Type = 1
FEATURE [PartDesign::Body] Body020  label="sink_material_0.30ansi"
  AllowCompound = false
  Group = -> [Sketch037,Line,DatumLine,Sketch038,DatumLine001,Sketch039,BaseBend011,Bend004,Local_CS,Sketch040,Binder031,Pocket022,Sketch041,Sketch042,Sketch219,Bend033,Pocket131,Mirrored017,Pocket024,Sketch043,CornerRelief,Pocket023,Mirrored002,Boolean008,Sketch064,Pocket029]
  Origin = -> Origin028
  Tip = -> Pocket029
COMPONENT P74 — recipe-attached ("pillar2", modeled in this document).
Construction recipe (the document's own serialized feature program — sketch geometry with constraints, then the solid features built on it; lengths are millimeters unless a unit is written):

FEATURE [Sketcher::SketchObject] Sketch180
  ArcFitTolerance = 0
  AttachmentSupport = -> [YZ_Plane085]
  FullyConstrained = true
  MakeInternals = false
  MapMode = 5
  Placement = pos=(0,0,0) rot=(0.57735,0.57735,0.57735;2.0944rad)
  sketch-geometry (4):
    g0: ArcOfCircle CenterX=-4 CenterY=4 CenterZ=0 NormalX=0 NormalY=0 NormalZ=1 AngleXU=0 Radius=4 StartAngle=4.71239 EndAngle=6.28319
    g1: ArcOfCircle CenterX=-4 CenterY=4 CenterZ=0 NormalX=0 NormalY=0 NormalZ=1 AngleXU=0 Radius=2 StartAngle=4.71239 EndAngle=6.28319
    g2: LineSegment StartX=-4 StartY=0 StartZ=0 EndX=-4 EndY=2 EndZ=0
    g3: LineSegment StartX=-2 StartY=4 StartZ=0 EndX=0 EndY=4 EndZ=0
  constraints (13):
    c: PointOnObject(g0,g-1)
    c: PointOnObject(g0,g-2)
    c: Coincident(g1,g0)
    c: Coincident(g2,g0)
    c: Coincident(g2,g1)
    c: Coincident(g3,g1)
    c: Coincident(g3,g0)
    c: Perpendicular(g1,g3)
    c: Perpendicular(g1,g2)
    c: Vertical(g2)
    c: Horizontal(g3)
    c: Radius(g1) = 2  'r'
    c: Distance(g2) = 2  'thickness'
FEATURE [PartDesign::Pad] Pad020
  Direction = (1,0,0)
  Length = 101
  Length2 = 10
  Midplane = true
  Placement = pos=(0,0,0) rot=(1,1,1;2.0944rad)
  Profile = -> Sketch180
  ReferenceAxis = -> Sketch180 [N_Axis]
  Suppressed = false
  Type = 0
FEATURE [Sketcher::SketchObject] Sketch181
  ArcFitTolerance = 0
  AttachmentSupport = -> [XY_Plane085]
  FullyConstrained = true
  MakeInternals = false
  MapMode = 5
  expr: Constraints[2] = Pad020.Length
  sketch-geometry (4):
    g0: LineSegment StartX=-50.5 StartY=-4 StartZ=0 EndX=50.5 EndY=-4 EndZ=0
    g1: LineSegment StartX=29.5 StartY=-25 StartZ=0 EndX=-29.5 EndY=-25 EndZ=0
    g2: ArcOfCircle CenterX=29.5 CenterY=-4 CenterZ=0 NormalX=0 NormalY=0 NormalZ=1 AngleXU=0 Radius=21 StartAngle=4.71239 EndAngle=6.28319
    g3: ArcOfCircle CenterX=-29.5 CenterY=-4 CenterZ=0 NormalX=0 NormalY=0 NormalZ=1 AngleXU=0 Radius=21 StartAngle=3.14159 EndAngle=4.71239
  constraints (11):
    c: Horizontal(g1)
    c: DistanceY(g0) = -4
    c: DistanceX(g0,g0) = 101
    c: DistanceY(g1,g-1) = 25
    c: PointOnObject(g2,g0)
    c: Coincident(g2,g0)
    c: PointOnObject(g3,g0)
    c: Coincident(g3,g0)
    c: Tangent(g3,g1) = 1.5708
    c: Tangent(g2,g1) = 1.5708
    c: Symmetric(g0,g0,g-2)
FEATURE [Sketcher::SketchObject] Sketch182
  ArcFitTolerance = 0
  AttachmentSupport = -> [XZ_Plane085]
  FullyConstrained = true
  MakeInternals = false
  MapMode = 5
  Placement = pos=(0,0,0) rot=(1,0,0;1.5708rad)
  expr: Constraints[17] = <<pillar2_base_sketch>>.Constraints.length + 3 mm
  expr: Constraints[8] = Pad020.Length
  sketch-geometry (13):
    g0: LineSegment StartX=-50.5 StartY=4 StartZ=0 EndX=-50.5 EndY=110 EndZ=0
    g1: LineSegment StartX=-35.5 StartY=110 StartZ=0 EndX=-35.5 EndY=66.1722 EndZ=0
    g2: LineSegment StartX=-18.1011 StartY=38.947 StartZ=0 EndX=47.6002 EndY=8.53754 EndZ=0
    g3: ArcOfCircle CenterX=45.5 CenterY=4 CenterZ=0 NormalX=0 NormalY=0 NormalZ=1 AngleXU=0 Radius=5 StartAngle=2.92426e-11 EndAngle=1.13731
    g4: ArcOfCircle CenterX=-5.5 CenterY=66.1722 CenterZ=0 NormalX=0 NormalY=0 NormalZ=1 AngleXU=0 Radius=30 StartAngle=3.14159 EndAngle=4.27891
    g5: GeomPoint [constr] X=-35.5 Y=47 Z=0
    g6: GeomPoint [constr] X=-35.5 Y=110 Z=0
    g7: GeomPoint [constr] X=-52.5 Y=110 Z=0
    g8: LineSegment StartX=50.5 StartY=4 StartZ=0 EndX=-48.5 EndY=4 EndZ=0
    g9: LineSegment StartX=-48.5 StartY=4 StartZ=0 EndX=-50.5 EndY=4 EndZ=0
    g10: LineSegment StartX=-50.5 StartY=110 StartZ=0 EndX=-48.5 EndY=110 EndZ=0
    g11: LineSegment StartX=-48.5 StartY=110 StartZ=0 EndX=-35.5 EndY=110 EndZ=0
    g12: LineSegment [constr] StartX=-48.5 StartY=4 StartZ=0 EndX=-48.5 EndY=110 EndZ=0
  constraints (32):
    c: Vertical(g0)
    c: Coincident(g0,g10)
    c: Vertical(g1)
    c: Coincident(g9,g0)
    c: Coincident(g3,g8)
    c: Tangent(g3,g2) = 1.5708
    c: DistanceY(g8) = 4
    c: Symmetric(g0,g8,g-2)
    c: DistanceX(g9,g8) = 101
    c: DistanceY(g0) = 110  'total_height'
    c: PointOnObject(g5,g1)
    c: PointOnObject(g5,g2)
    c: Tangent(g1,g4) = -1.5708
    c: Tangent(g2,g4) = -1.5708
    c: Radius(g4) = 30
    c: Radius(g3) = 5
    c: DistanceX(g7,g0) = 2
    c: DistanceX(g7,g6) = 17
    c: Coincident(g8,g9)
    c: PointOnObject(g3,g8)
    c: Coincident(g10,g11)
    c: Horizontal(g10)
    c: Horizontal(g11)
    c: PointOnObject(g7,g10)
    c: Coincident(g12,g8)
    c: Coincident(g12,g11)
    c: Vertical(g12)
    c: DistanceX(g0,g11) = 2
    c: Horizontal(g9)
    c: DistanceY(g5) = 47
    c: Coincident(g1,g11)
    c: Coincident(g1,g6)
FEATURE [PartDesign::Pad] Pad021
  BaseFeature = -> Pad020
  Direction = (0,0,1)
  Length = 2
  Length2 = 10
  Placement = pos=(0,0,0) rot=(1,1,1;2.0944rad)
  Profile = -> Sketch181
  ReferenceAxis = -> Sketch181 [N_Axis]
  Suppressed = false
  Type = 0
FEATURE [PartDesign::Pad] Pad022
  BaseFeature = -> Pad021
  Direction = (0,-1,2e-16)
  Length = 2
  Length2 = 10
  Placement = pos=(0,0,0) rot=(1,1,1;2.0944rad)
  Profile = -> Sketch182
  ReferenceAxis = -> Sketch182 [N_Axis]
  Suppressed = false
  Type = 0
FEATURE [Sketcher::SketchObject] Sketch183
  ArcFitTolerance = 0
  AttachmentOffset = pos=(-52.5,2,0) rot=(0,0,1;0rad)
  AttachmentSupport = -> [XY_Plane085]
  FullyConstrained = true
  MakeInternals = false
  MapMode = 5
  Placement = pos=(-52.5,2,0) rot=(0,0,1;0rad)
  expr: .AttachmentOffset.Base.x = -Pad020.Length / 2 - 2 mm
  expr: Constraints[16] = <<pillar2_base_sketch>>.Constraints.width / 2 - 1 mm
  sketch-geometry (9):
    g0: ArcOfCircle CenterX=-5.92e-14 CenterY=4.503e-13 CenterZ=0 NormalX=0 NormalY=0 NormalZ=1 AngleXU=0 Radius=2 StartAngle=3.14159 EndAngle=4.71239
    g1: ArcOfCircle CenterX=-5.92e-14 CenterY=4.503e-13 CenterZ=0 NormalX=0 NormalY=0 NormalZ=1 AngleXU=0 Radius=4 StartAngle=3.14159 EndAngle=4.71239
    g2: LineSegment StartX=-2 StartY=-4.474e-13 StartZ=0 EndX=-2 EndY=15.3 EndZ=0
    g3: LineSegment StartX=-2 StartY=15.3 StartZ=0 EndX=-4 EndY=15.3 EndZ=0
    g4: LineSegment StartX=-4 StartY=15.3 StartZ=0 EndX=-4 EndY=0 EndZ=0
    g5: LineSegment [constr] StartX=5e-16 StartY=-4 StartZ=0 EndX=8e-16 EndY=-2 EndZ=0
    g6: LineSegment StartX=5e-16 StartY=-4 StartZ=0 EndX=2 EndY=-4 EndZ=0
    g7: LineSegment StartX=2 StartY=-4 StartZ=0 EndX=2 EndY=-2 EndZ=0
    g8: LineSegment StartX=2 StartY=-2 StartZ=0 EndX=9e-16 EndY=-2 EndZ=0
  constraints (25):
    c: Coincident(g0,g-1)
    c: PointOnObject(g0,g-2)
    c: PointOnObject(g0,g-1)
    c: Coincident(g1,g0)
    c: PointOnObject(g1,g-2)
    c: PointOnObject(g1,g-1)
    c: Tangent(g0,g2) = 1.5708
    c: Coincident(g2,g3)
    c: Horizontal(g3)
    c: Coincident(g3,g4)
    c: Coincident(g4,g1)
    c: Vertical(g4)
    c: Coincident(g5,g1)
    c: Coincident(g5,g0)
    c: Radius(g0) = 2
    c: DistanceY(g5,g5) = 2
    c: DistanceY(g0,g2) = 17.3
    c: Coincident(g6,g7)
    c: Coincident(g7,g8)
    c: Horizontal(g6)
    c: Horizontal(g8)
    c: Vertical(g7)
    c: Coincident(g6,g1)
    c: Coincident(g0,g8)
    c: DistanceX(g6,g6) = 2
FEATURE [Sketcher::SketchObject] Sketch184
  ArcFitTolerance = 0
  AttachmentSupport = -> [YZ_Plane085]
  ExternalGeometry = -> [Sketch183]
  FullyConstrained = true
  MakeInternals = false
  MapMode = 5
  Placement = pos=(0,0,0) rot=(0.57735,0.57735,0.57735;2.0944rad)
  expr: Constraints[12] = Sketch182.Constraints.total_height
  sketch-geometry (9):
    g0: ArcOfCircle CenterX=15.3 CenterY=2 CenterZ=0 NormalX=0 NormalY=0 NormalZ=1 AngleXU=0 Radius=2 StartAngle=4.71239 EndAngle=6.28319
    g1: LineSegment StartX=17.3 StartY=2 StartZ=0 EndX=17.3 EndY=1.47e-14 EndZ=0
    g2: LineSegment StartX=17.3 StartY=1.47e-14 StartZ=0 EndX=15.3 EndY=1.95e-14 EndZ=0
    g3: LineSegment StartX=17.3 StartY=108 StartZ=0 EndX=17.3 EndY=110 EndZ=0
    g4: LineSegment StartX=17.3 StartY=110 StartZ=0 EndX=15.3 EndY=110 EndZ=0
    g5: ArcOfCircle CenterX=15.3 CenterY=108 CenterZ=0 NormalX=0 NormalY=0 NormalZ=1 AngleXU=0 Radius=2 StartAngle=-5.3e-15 EndAngle=1.5708
    g6: ArcOfCircle CenterX=4 CenterY=2 CenterZ=0 NormalX=0 NormalY=0 NormalZ=1 AngleXU=0 Radius=2 StartAngle=3.14159 EndAngle=4.71239
    g7: LineSegment StartX=2 StartY=2 StartZ=0 EndX=2 EndY=1.11e-14 EndZ=0
    g8: LineSegment StartX=2 StartY=1.11e-14 StartZ=0 EndX=4 EndY=3.55e-14 EndZ=0
  constraints (22):
    c: Coincident(g1,g2)
    c: Vertical(g3)
    c: Coincident(g3,g4)
    c: Horizontal(g4)
    c: Tangent(g5,g4) = -1.5708
    c: Tangent(g5,g3) = -1.5708
    c: Vertical(g1)
    c: Tangent(g0,g1) = 1.5708
    c: Tangent(g2,g0) = 1.5708
    c: Vertical(g3,g1)
    c: Equal(g5,g0)
    c: Radius(g5) = 2
    c: DistanceY(g3) = 110
    c: Coincident(g7,g8)
    c: Vertical(g7)
    c: Tangent(g6,g7) = -1.5708
    c: Tangent(g8,g6) = -1.5708
    c: Equal(g6,g0)
    c: Coincident(g1,g-3)
    c: Coincident(g7,g-3)
    c: PointOnObject(g6,g-3)
    c: PointOnObject(g0,g-1)
FEATURE [Sketcher::SketchObject] Sketch185
  ArcFitTolerance = 0
  AttachmentOffset = pos=(-52.5,2,0) rot=(0,0,1;0rad)
  AttachmentSupport = -> [XY_Plane085]
  FullyConstrained = true
  MakeInternals = false
  MapMode = 5
  Placement = pos=(-52.5,2,0) rot=(0,0,1;0rad)
  expr: AttachmentOffset = <<Sketch183>>.AttachmentOffset
  sketch-geometry (6):
    g0: ArcOfCircle CenterX=-1.4879e-12 CenterY=3.7497e-12 CenterZ=0 NormalX=0 NormalY=0 NormalZ=1 AngleXU=0 Radius=4 StartAngle=3.14159 EndAngle=4.71239
    g1: ArcOfCircle CenterX=-1.4879e-12 CenterY=3.7497e-12 CenterZ=0 NormalX=0 NormalY=0 NormalZ=1 AngleXU=0 Radius=2 StartAngle=3.14159 EndAngle=4.71239
    g2: LineSegment StartX=-4 StartY=-4.94e-14 StartZ=0 EndX=-2 EndY=-2.158e-13 EndZ=0
    g3: LineSegment StartX=1.1155e-12 StartY=-4 StartZ=0 EndX=2 EndY=-4 EndZ=0
    g4: LineSegment StartX=2 StartY=-4 StartZ=0 EndX=2 EndY=-2 EndZ=0
    g5: LineSegment StartX=2 StartY=-2 StartZ=0 EndX=1.583e-13 EndY=-2 EndZ=0
  constraints (17):
    c: Coincident(g0,g-1)
    c: PointOnObject(g0,g-2)
    c: PointOnObject(g0,g-1)
    c: Coincident(g1,g0)
    c: PointOnObject(g1,g-2)
    c: PointOnObject(g1,g-1)
    c: Coincident(g2,g0)
    c: Coincident(g2,g1)
    c: Radius(g1) = 2
    c: Radius(g0) = 4
    c: Tangent(g0,g3) = -1.5708
    c: Coincident(g3,g4)
    c: Vertical(g4)
    c: Coincident(g4,g5)
    c: Coincident(g5,g1)
    c: Horizontal(g5)
    c: DistanceX(g5,g5) = 2
FEATURE [Sketcher::SketchObject] Sketch186  label="pillar2_base_sketch"
  ArcFitTolerance = 0
  AttachmentSupport = -> [XY_Plane086]
  FullyConstrained = true
  MakeInternals = false
  MapMode = 5
  expr: .Constraints.length = <<pillar2_Properties>>.outer_length
  sketch-geometry (5):
    g0: LineSegment StartX=-18.3 StartY=14 StartZ=0 EndX=-18.3 EndY=0 EndZ=0
    g1: LineSegment StartX=-18.3 StartY=0 StartZ=0 EndX=18.3 EndY=0 EndZ=0
    g2: LineSegment StartX=18.3 StartY=0 StartZ=0 EndX=18.3 EndY=14 EndZ=0
    g3: LineSegment [constr] StartX=18.3 StartY=14 StartZ=0 EndX=-18.3 EndY=14 EndZ=0
    g4: GeomPoint [constr] X=0 Y=7 Z=0
  constraints (13):
    c: Coincident(g0,g1)
    c: Coincident(g1,g2)
    c: Coincident(g2,g3)
    c: Coincident(g3,g0)
    c: Horizontal(g1)
    c: Horizontal(g3)
    c: Vertical(g0)
    c: Vertical(g2)
    c: Symmetric(g1,g0,g4)
    c: PointOnObject(g4,g-2)
    c: PointOnObject(g1,g-1)
    c: DistanceX(g1,g1) = 36.6  'width'
    c: DistanceY(g2,g2) = 14  'length'
FEATURE [PartDesign::FeaturePython] BaseBend045  # WARN: FeaturePython — macro-defined, semantics opaque (R4)
  BendSide = 1
  BendSketch = -> Sketch186
  MidPlane = false
  Reverse = false
  Suppressed = false
  length = 1596
  radius = 2
  thickness = 2
FEATURE [Sketcher::SketchObject] Sketch187
  ArcFitTolerance = 0
  AttachmentOffset = pos=(0,1598,0) rot=(0,0,1;0rad)
  AttachmentSupport = -> [XZ_Plane086]
  FullyConstrained = true
  MakeInternals = false
  MapMode = 5
  Placement = pos=(0,3.548e-13,1598) rot=(1,0,0;1.5708rad)
  expr: .AttachmentOffset.Base.y = BaseBend045.length + Sketch188.Constraints.length
  expr: Constraints[11] = <<pillar2_Properties>>.outer_width - 4 mm * 2 + (<<pillar2_Properties>>.outer_length - 4 mm) * 2 + 9.42 mm
  sketch-geometry (5):
    g0: LineSegment StartX=-29.01 StartY=88 StartZ=0 EndX=-29.01 EndY=0 EndZ=0
    g1: LineSegment StartX=-29.01 StartY=0 StartZ=0 EndX=29.01 EndY=0 EndZ=0
    g2: LineSegment StartX=29.01 StartY=0 StartZ=0 EndX=29.01 EndY=88 EndZ=0
    g3: LineSegment StartX=29.01 StartY=88 StartZ=0 EndX=-29.01 EndY=88 EndZ=0
    g4: GeomPoint [constr] X=0 Y=44 Z=0
  constraints (13):
    c: Coincident(g0,g1)
    c: Coincident(g1,g2)
    c: Coincident(g2,g3)
    c: Coincident(g3,g0)
    c: Horizontal(g1)
    c: Horizontal(g3)
    c: Vertical(g0)
    c: Vertical(g2)
    c: Symmetric(g1,g0,g4)
    c: PointOnObject(g4,g-2)
    c: PointOnObject(g1,g-1)
    c: DistanceX(g1,g1) = 58.02
    c: DistanceY(g2,g2) = 88
FEATURE [Sketcher::SketchObject] Sketch188
  ArcFitTolerance = 0
  AttachmentOffset = pos=(0,1596,0) rot=(0,0,1;0rad)
  AttachmentSupport = -> [XZ_Plane086]
  FullyConstrained = true
  MakeInternals = false
  MapMode = 5
  Placement = pos=(0,3.544e-13,1596) rot=(1,0,0;1.5708rad)
  expr: .AttachmentOffset.Base.y = BaseBend045.length
  expr: Constraints[11] = <<pillar2_Properties>>.outer_width - (<<pillar2_Properties>>.thickness + <<pillar2_Properties>>.default_bend_r) * 2
  sketch-geometry (7):
    g0: LineSegment [constr] StartX=-14.3 StartY=2 StartZ=0 EndX=-14.3 EndY=-4e-16 EndZ=0
    g1: LineSegment StartX=-14.3 StartY=-4e-16 StartZ=0 EndX=14.3 EndY=-4e-16 EndZ=0
    g2: LineSegment [constr] StartX=14.3 StartY=-4e-16 StartZ=0 EndX=14.3 EndY=2 EndZ=0
    g3: LineSegment StartX=14.3 StartY=2 StartZ=0 EndX=-14.3 EndY=2 EndZ=0
    g4: GeomPoint [constr] X=-2.547e-12 Y=1 Z=0
    g5: ArcOfCircle CenterX=14.3 CenterY=1 CenterZ=0 NormalX=0 NormalY=0 NormalZ=1 AngleXU=0 Radius=1 StartAngle=1.5708 EndAngle=4.71239
    g6: ArcOfCircle CenterX=-14.3 CenterY=1 CenterZ=0 NormalX=0 NormalY=0 NormalZ=1 AngleXU=0 Radius=1 StartAngle=4.71239 EndAngle=7.85398
  constraints (19):
    c: Coincident(g0,g1)
    c: Coincident(g1,g2)
    c: Coincident(g2,g3)
    c: Coincident(g3,g0)
    c: Horizontal(g1)
    c: Horizontal(g3)
    c: Vertical(g0)
    c: Vertical(g2)
    c: Symmetric(g1,g0,g4)
    c: PointOnObject(g4,g-2)
    c: PointOnObject(g1,g-1)
    c: DistanceX(g1,g1) = 28.6
    c: DistanceY(g2) = 2  'length'
    c: PointOnObject(g5,g2)
    c: Coincident(g5,g1)
    c: Coincident(g5,g3)
    c: PointOnObject(g6,g0)
    c: Coincident(g6,g1)
    c: Coincident(g6,g3)
FEATURE [PartDesign::Pad] Pad024
  BaseFeature = -> BaseBend045
  Direction = (0,-1,2e-16)
  Length = 2
  Length2 = 10
  Profile = -> Sketch188
  ReferenceAxis = -> Sketch188 [N_Axis]
  Reversed = true
  Suppressed = false
  Type = 0
FEATURE [PartDesign::Pad] Pad025
  BaseFeature = -> Pad024
  Direction = (0,-1,2e-16)
  Length = 2
  Length2 = 10
  Profile = -> Sketch187
  ReferenceAxis = -> Sketch187 [N_Axis]
  Reversed = true
  Suppressed = false
  Type = 0
FEATURE [Sketcher::SketchObject] Sketch189
  ArcFitTolerance = 0
  AttachmentSupport = -> [XZ_Plane086]
  ExternalGeometry = -> [Sketch187]
  FullyConstrained = true
  MakeInternals = false
  MapMode = 5
  Placement = pos=(0,0,0) rot=(1,0,0;1.5708rad)
  sketch-geometry (12):
    g0: LineSegment StartX=26.01 StartY=1598 StartZ=0 EndX=29.01 EndY=1598 EndZ=0
    g1: LineSegment StartX=29.01 StartY=1598 StartZ=0 EndX=29.01 EndY=1601 EndZ=0
    g2: LineSegment StartX=29.01 StartY=1683 StartZ=0 EndX=29.01 EndY=1686 EndZ=0
    g3: LineSegment StartX=29.01 StartY=1686 StartZ=0 EndX=26.01 EndY=1686 EndZ=0
    g4: LineSegment StartX=-26.01 StartY=1686 StartZ=0 EndX=-29.01 EndY=1686 EndZ=0
    g5: LineSegment StartX=-29.01 StartY=1686 StartZ=0 EndX=-29.01 EndY=1683 EndZ=0
    g6: LineSegment StartX=-29.01 StartY=1601 StartZ=0 EndX=-29.01 EndY=1598 EndZ=0
    g7: LineSegment StartX=-29.01 StartY=1598 StartZ=0 EndX=-26.01 EndY=1598 EndZ=0
    g8: ArcOfCircle CenterX=26.01 CenterY=1601 CenterZ=0 NormalX=0 NormalY=0 NormalZ=1 AngleXU=0 Radius=3 StartAngle=4.71239 EndAngle=6.28319
    g9: ArcOfCircle CenterX=26.01 CenterY=1683 CenterZ=0 NormalX=0 NormalY=0 NormalZ=1 AngleXU=0 Radius=3 StartAngle=-2.04e-14 EndAngle=1.5708
    g10: ArcOfCircle CenterX=-26.01 CenterY=1683 CenterZ=0 NormalX=0 NormalY=0 NormalZ=1 AngleXU=0 Radius=3 StartAngle=1.5708 EndAngle=3.14159
    g11: ArcOfCircle CenterX=-26.01 CenterY=1601 CenterZ=0 NormalX=0 NormalY=0 NormalZ=1 AngleXU=0 Radius=3 StartAngle=3.14159 EndAngle=4.71239
  constraints (29):
    c: Coincident(g0,g-3)
    c: Horizontal(g0)
    c: Coincident(g0,g1)
    c: PointOnObject(g1,g-3)
    c: PointOnObject(g2,g-3)
    c: Coincident(g2,g-3)
    c: Coincident(g2,g3)
    c: Horizontal(g3)
    c: Coincident(g4,g-4)
    c: Horizontal(g4)
    c: Coincident(g4,g5)
    c: PointOnObject(g5,g-4)
    c: PointOnObject(g6,g-4)
    c: Coincident(g6,g-4)
    c: Coincident(g6,g7)
    c: Horizontal(g7)
    c: Coincident(g9,g3)
    c: Tangent(g8,g0) = -1.5708
    c: Tangent(g8,g1) = -1.5708
    c: Tangent(g9,g2) = -1.5708
    c: Tangent(g9,g3,g3) = -1.5708
    c: Tangent(g10,g4) = -1.5708
    c: Tangent(g10,g5) = -1.5708
    c: Tangent(g11,g7) = -1.5708
    c: Tangent(g11,g6) = -1.5708
    c: Equal(g8,g9)
    c: Equal(g8,g10)
    c: Equal(g8,g11)
    c: Radius(g8) = 3
FEATURE [PartDesign::Pocket] Pocket115
  BaseFeature = -> Pad025
  Direction = (0,1,-2e-16)
  Length = 5
  Length2 = 5
  Profile = -> Sketch189
  ReferenceAxis = -> Sketch189 [N_Axis]
  Suppressed = false
  Type = 1
FEATURE [Sketcher::SketchObject] Sketch190
  ArcFitTolerance = 0
  AttachmentOffset = pos=(14,0,0) rot=(0,0,1;0rad)
  AttachmentSupport = -> [YZ_Plane086]
  FullyConstrained = true
  MakeInternals = false
  MapMode = 5
  Placement = pos=(0,14,0) rot=(0.57735,0.57735,0.57735;2.0944rad)
  expr: .AttachmentOffset.Base.x = <<pillar2_Properties>>.outer_length
  sketch-geometry (3):
    g0: ArcOfCircle CenterX=-3 CenterY=3 CenterZ=0 NormalX=0 NormalY=0 NormalZ=1 AngleXU=0 Radius=3 StartAngle=4.71239 EndAngle=6.28319
    g1: LineSegment StartX=-5.6e-14 StartY=3 StartZ=0 EndX=-5.6e-14 EndY=0 EndZ=0
    g2: LineSegment StartX=-5.6e-14 StartY=0 StartZ=0 EndX=-3 EndY=6.7e-15 EndZ=0
  constraints (7):
    c: PointOnObject(g0,g-1)
    c: Coincident(g2,g1)
    c: Vertical(g1)
    c: Tangent(g0,g1) = 1.5708
    c: Tangent(g2,g0) = 1.5708
    c: Coincident(g1,g-1)
    c: Radius(g0) = 3
FEATURE [PartDesign::Pocket] Pocket116
  BaseFeature = -> Pocket115
  Direction = (-1,0,0)
  Length = 5
  Length2 = 5
  Midplane = true
  Profile = -> Sketch190
  ReferenceAxis = -> Sketch190 [N_Axis]
  Suppressed = false
  Type = 1
FEATURE [PartDesign::Plane] DatumPlane006
  AttachmentOffset = pos=(0,0,798) rot=(1,0,0;0rad)
  AttachmentSupport = -> [XY_Plane086]
  Length = 68.7922
  MapMode = 5
  Placement = pos=(0,0,798) rot=(0,0,1;0rad)
  ResizeMode = 0
  Width = 60.7722
  expr: .AttachmentOffset.Base.z = BaseBend045.length / 2
FEATURE [PartDesign::Mirrored] Mirrored013
  BaseFeature = -> Pocket116
  MirrorPlane = -> DatumPlane006
  Originals = -> [Pocket116]
  Suppressed = false
  TransformMode = 0
FEATURE [Sketcher::SketchObject] Sketch192
  ArcFitTolerance = 0
  AttachmentSupport = -> [XZ_Plane085]
  FullyConstrained = true
  MakeInternals = false
  MapMode = 5
  Placement = pos=(0,0,0) rot=(1,0,0;1.5708rad)
  sketch-geometry (4):
    g0: LineSegment StartX=-46.5 StartY=-2.18e-14 StartZ=0 EndX=-50.5 EndY=-2.18e-14 EndZ=0
    g1: LineSegment StartX=-50.5 StartY=-2.18e-14 StartZ=0 EndX=-50.5 EndY=4 EndZ=0
    g2: LineSegment StartX=-50.5 StartY=4 StartZ=0 EndX=-46.5 EndY=4 EndZ=0
    g3: LineSegment StartX=-46.5 StartY=4 StartZ=0 EndX=-46.5 EndY=-2.18e-14 EndZ=0
  constraints (12):
    c: Coincident(g0,g1)
    c: Coincident(g1,g2)
    c: Coincident(g2,g3)
    c: Coincident(g3,g0)
    c: Horizontal(g0)
    c: Horizontal(g2)
    c: Vertical(g1)
    c: Vertical(g3)
    c: PointOnObject(g0,g-1)
    c: DistanceX(g0,g0) = 4
    c: Equal(g1,g0)
    c: DistanceX(g0) = -50.5
FEATURE [Sketcher::SketchObject] Sketch194
  ArcFitTolerance = 0
  AttachmentSupport = -> [XZ_Plane085]
  FullyConstrained = true
  MakeInternals = false
  MapMode = 5
  Placement = pos=(0,0,0) rot=(1,0,0;1.5708rad)
  sketch-geometry (6):
    g0: LineSegment StartX=-50.5 StartY=108 StartZ=0 EndX=-50.5 EndY=110 EndZ=0
    g1: LineSegment StartX=-50.5 StartY=110 StartZ=0 EndX=-48.5 EndY=110 EndZ=0
    g2: LineSegment StartX=-43.5 StartY=110 StartZ=0 EndX=-35.5 EndY=110 EndZ=0
    g3: LineSegment StartX=-35.5 StartY=110 StartZ=0 EndX=-35.5 EndY=102 EndZ=0
    g4: ArcOfCircle CenterX=-43.5 CenterY=102 CenterZ=0 NormalX=0 NormalY=0 NormalZ=1 AngleXU=0 Radius=8 StartAngle=8.302e-13 EndAngle=1.5708
    g5: ArcOfCircle CenterX=-48.5 CenterY=108 CenterZ=0 NormalX=0 NormalY=0 NormalZ=1 AngleXU=0 Radius=2 StartAngle=1.5708 EndAngle=3.14159
  constraints (16):
    c: Vertical(g0)
    c: Coincident(g0,g1)
    c: Horizontal(g1)
    c: Horizontal(g2)
    c: Coincident(g2,g3)
    c: Vertical(g3)
    c: Horizontal(g0,g2)
    c: DistanceY(g0) = 110
    c: Tangent(g5,g0) = 1.5708
    c: DistanceX(g0) = -50.5
    c: Tangent(g5,g1) = 1.5708
    c: Tangent(g4,g3) = 1.5708
    c: Tangent(g4,g2) = 1.5708
    c: DistanceX(g0,g2) = 15
    c: DistanceX(g0,g2) = 7
    c: Radius(g5) = 2
FEATURE [PartDesign::Pocket] Pocket119
  BaseFeature = -> Pad022
  Direction = (0,1,-2e-16)
  Length = 5
  Length2 = 5
  Midplane = true
  Placement = pos=(0,0,0) rot=(1,1,1;2.0944rad)
  Profile = -> Sketch194
  ReferenceAxis = -> Sketch194 [N_Axis]
  Suppressed = false
  Type = 1
FEATURE [PartDesign::Boolean] Boolean015
  BaseFeature = -> Pocket119
  Group = -> [Compound054]
  Refine = true
  Suppressed = false
  Type = 1
  UsePlacement = false
FEATURE [PartDesign::Body] Body111  label="pillar2_bottom_material_0.50ansi"
  AllowCompound = false
  Group = -> [Sketch180,Pad020,Sketch181,Sketch182,Sketch192,Pad021,Pad022,Sketch183,Sketch184,Sketch185,Pocket119,Boolean015,Sketch194]
  Origin = -> Origin085
  Placement = pos=(18.3,54.5,0) rot=(0,0,1;1.5708rad)
  Tip = -> Boolean015
FEATURE [PartDesign::Boolean] Boolean016
  BaseFeature = -> Mirrored013
  Group = -> [Compound052]
  Refine = true
  Suppressed = false
  Type = 1
  UsePlacement = false
FEATURE [PartDesign::Body] Body112  label="pillar2_material_0.50ansi"
  AllowCompound = false
  Group = -> [Sketch186,BaseBend045,Sketch187,Sketch188,Pad024,Pad025,Sketch189,Pocket115,Sketch190,Pocket116,DatumPlane006,Mirrored013,Boolean016]
  Origin = -> Origin086
  Tip = -> Boolean016
COMPONENT P75 — recipe-attached ("basement_v2", modeled in this document).
Construction recipe (the document's own serialized feature program — sketch geometry with constraints, then the solid features built on it; lengths are millimeters unless a unit is written):

FEATURE [PartDesign::SubShapeBinder] Binder123
  BindCopyOnChange = 0
  BindMode = 0
  ClaimChildren = true
  Context = -> Part020 [Body114.Binder123.]
  Fuse = false
  MakeFace = true
  OffsetFill = false
  OffsetIntersection = false
  OffsetJoinType = 0
  OffsetOpenResult = false
  PartialLoad = false
  Relative = true
  Support = -> [Array009]
  _Version = 2
FEATURE [PartDesign::Pad] Pad026
  Direction = (0,0,1)
  Length = 18
  Length2 = 10
  Profile = -> Binder123
  Refine = true
  Suppressed = false
  Type = 0
FEATURE [PartDesign::SubShapeBinder] Binder124
  BindCopyOnChange = 0
  BindMode = 0
  ClaimChildren = true
  Context = -> Part020 [Body116.Binder124.]
  Fuse = false
  MakeFace = true
  OffsetFill = false
  OffsetIntersection = false
  OffsetJoinType = 0
  OffsetOpenResult = false
  PartialLoad = false
  Relative = true
  Support = -> [Array003]
  _Version = 2
  expr: Support = Array003._self
FEATURE [PartDesign::Pad] Pad027
  Direction = (0,0,1)
  Length = 18
  Length2 = 10
  Profile = -> Binder124
  Suppressed = false
  Type = 0
FEATURE [PartDesign::SubShapeBinder] Binder125
  BindCopyOnChange = 0
  BindMode = 0
  ClaimChildren = true
  Context = -> Part020 [Body117.Binder125.]
  Fuse = false
  MakeFace = true
  OffsetFill = false
  OffsetIntersection = false
  OffsetJoinType = 0
  OffsetOpenResult = false
  PartialLoad = false
  Relative = false
  Support = -> [Array002]
  _Version = 2
FEATURE [PartDesign::Pad] Pad028
  Direction = (0,0,1)
  Length = 18
  Length2 = 10
  Profile = -> Binder125
  Suppressed = false
  Type = 0
FEATURE [Sketcher::SketchObject] Sketch204
  ArcFitTolerance = 0
  AttachmentOffset = pos=(0,370,0) rot=(0,0,1;0rad)
  AttachmentSupport = -> [XY_Plane092]
  FullyConstrained = true
  MakeInternals = false
  MapMode = 5
  Placement = pos=(0,370,0) rot=(0,0,1;0rad)
  sketch-geometry (1):
    g0: Circle CenterX=0 CenterY=0 CenterZ=0 NormalX=0 NormalY=0 NormalZ=1 AngleXU=0 Radius=4
  constraints (2):
    c: Coincident(g0,g-1)
    c: Diameter(g0) = 8
FEATURE [PartDesign::Hole] Hole021
  BaseFeature = -> Pad028
  CustomThreadClearance = 0
  Depth = 25
  DepthType = 0
  Diameter = 8
  DrillForDepth = false
  DrillPoint = 1
  DrillPointAngle = 118
  HoleCutCountersinkAngle = 90
  HoleCutCustomValues = false
  HoleCutDepth = 0
  HoleCutDiameter = 6.1
  HoleCutType = 0
  ModelThread = false
  Profile = -> Sketch204
  Reversed = true
  Suppressed = false
  Tapered = false
  TaperedAngle = 90
  ThreadClass = 0
  ThreadDepth = 25
  ThreadDepthType = 0
  ThreadDirection = 0
  ThreadFit = 0
  ThreadSize = 0
  ThreadType = 0
  Threaded = false
  UseCustomThreadClearance = false
FEATURE [PartDesign::PolarPattern] PolarPattern011
  Angle = 360
  Axis = -> Z_Axis092
  BaseFeature = -> Hole021
  Mode = 0
  Occurrences = 3
  Offset = 120
  Originals = -> [Hole021]
  Suppressed = false
  TransformMode = 0
FEATURE [PartDesign::Boolean] Boolean018
  BaseFeature = -> Pad026
  Group = -> [Fusion003]
  Suppressed = false
  Type = 1
  UsePlacement = false
FEATURE [PartDesign::Body] Body114  label="basement_v2_spacer"
  AllowCompound = false
  Group = -> [Binder123,Pad026,Boolean018]
  Origin = -> Origin089
  Tip = -> Boolean018
FEATURE [PartDesign::SubShapeBinder] Binder155
  BindCopyOnChange = 0
  BindMode = 0
  ClaimChildren = true
  Context = -> Part020 [Body156.Binder155.]
  Fuse = false
  MakeFace = true
  OffsetFill = false
  OffsetIntersection = false
  OffsetJoinType = 0
  OffsetOpenResult = false
  PartialLoad = false
  Relative = true
  Support = -> [Array009]
  _Version = 2
FEATURE [PartDesign::Pad] Pad052
  Direction = (0,0,1)
  Length = 18
  Length2 = 10
  Profile = -> Binder155
  Refine = true
  Suppressed = false
  Type = 0
FEATURE [PartDesign::Boolean] Boolean060
  BaseFeature = -> Pad052
  Group = -> [Fusion009]
  Suppressed = false
  Type = 1
  UsePlacement = false
FEATURE [PartDesign::Body] Body156  label="basement_v2_spacer001"
  AllowCompound = false
  Group = -> [Binder155,Pad052,Boolean060]
  Origin = -> Origin137
  Tip = -> Boolean060
FEATURE [PartDesign::Boolean] Boolean058
  BaseFeature = -> Pad027
  Group = -> [Fusion004]
  Suppressed = false
  Type = 1
  UsePlacement = true
FEATURE [PartDesign::Body] Body116  label="basement_v2_top"
  AllowCompound = false
  Group = -> [Binder124,Pad027,Boolean058]
  Origin = -> Origin091
  Tip = -> Boolean058
FEATURE [PartDesign::Boolean] Boolean019
  BaseFeature = -> PolarPattern011
  Group = -> [Fusion005]
  Suppressed = false
  Type = 1
  UsePlacement = false
FEATURE [PartDesign::Body] Body117  label="basement_v2_bottom"
  AllowCompound = false
  Group = -> [Binder125,Pad028,Sketch204,Hole021,PolarPattern011,Boolean019]
  Origin = -> Origin092
  Tip = -> Boolean019
PROVENANCE & LICENSES
A FreeCAD (.FCStd) document from a public repository crawl; recipes are the document's own serialized feature recipes (and, for linked parts, companion documents' recipes).
License: as declared in the source repository (recorded in the dataset sidecar).
